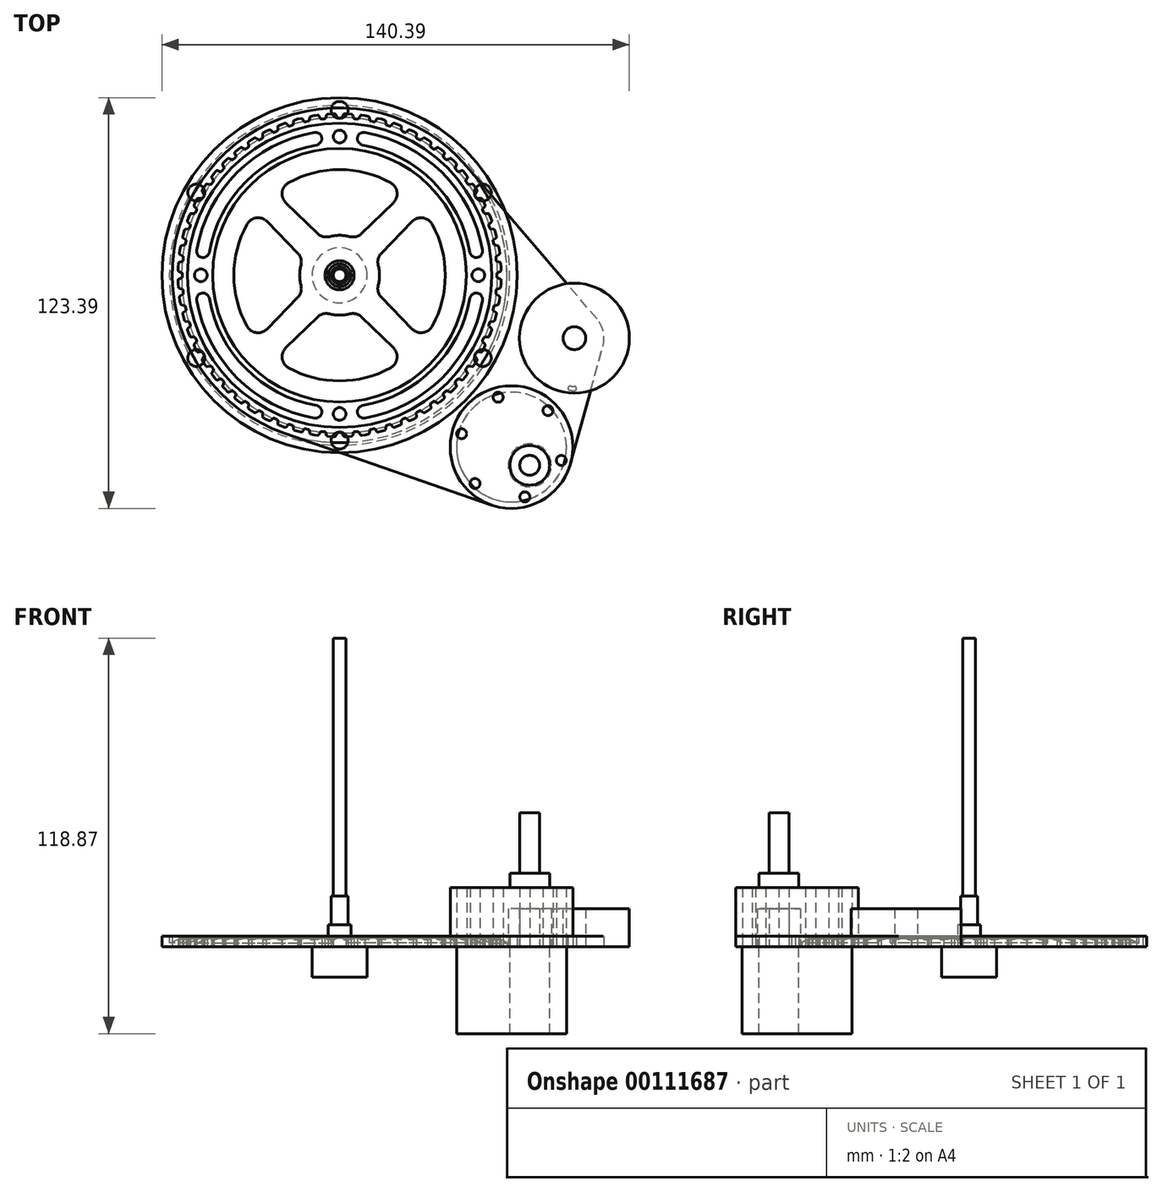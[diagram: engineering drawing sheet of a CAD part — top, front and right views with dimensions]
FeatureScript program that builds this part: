
annotation { "Feature Type Name" : "Feature", "Feature Type Description" : "" }
export const myFeature = defineFeature(function(context is Context, id is Id, definition is map)
    precondition{}
    {
        {
            var Q0;
            Q0=qCreatedBy(makeId("Top.planeOp"),FACE);
            var sketch = newSketch(context, id + "F0", { "sketchPlane" : qUnion([Q0])});
            skCircle(sketch, "E0", {"center": v(0, 0) * mm, "radius": 38.1 * mm});
            skCircle(sketch, "E1.0", {"center": v(0, 0) * mm, "radius": 45.72 * mm});
            skCircle(sketch, "E2", {"center": v(0, 41.68) * mm, "radius": 1.9 * mm});
            skArc(sketch, "E3.1.0", {"start": v(7.57, 42.92) * mm, "mid": v(5.36, 41.38) * mm, "end": v(6.9, 39.17) * mm});
            skLineSegment(sketch, "E3.anchor1", {"start": v(0, 0) * mm, "end": v(0, 41.68) * mm, "construction": true});
            skLineSegment(sketch, "E3.anchor2", {"start": v(0, 0) * mm, "end": v(7.24, 41.05) * mm, "construction": true});
            skArc(sketch, "E4.1.0", {"start": v(39.17, 6.9) * mm, "mid": v(41.38, 5.36) * mm, "end": v(42.92, 7.57) * mm});
            skLineSegment(sketch, "E4.anchor2", {"start": v(0, 0) * mm, "end": v(41.05, 7.24) * mm, "construction": true});
            skArc(sketch, "E5", {"start": v(7.57, 42.92) * mm, "mid": v(30.82, 30.82) * mm, "end": v(42.92, 7.57) * mm});
            skArc(sketch, "E6", {"start": v(6.9, 39.17) * mm, "mid": v(28.12, 28.12) * mm, "end": v(39.17, 6.9) * mm});
            skCircle(sketch, "E7.1.0", {"center": v(-41.68, 0) * mm, "radius": 1.9 * mm});
            skArc(sketch, "E7.1.1", {"start": v(-39.17, 6.9) * mm, "mid": v(-28.12, 28.12) * mm, "end": v(-6.9, 39.17) * mm});
            skArc(sketch, "E7.1.2", {"start": v(-42.92, 7.57) * mm, "mid": v(-30.82, 30.82) * mm, "end": v(-7.57, 42.92) * mm});
            skArc(sketch, "E7.1.3", {"start": v(-42.92, 7.57) * mm, "mid": v(-41.38, 5.36) * mm, "end": v(-39.17, 6.9) * mm});
            skArc(sketch, "E7.1.4", {"start": v(-6.9, 39.17) * mm, "mid": v(-5.36, 41.38) * mm, "end": v(-7.57, 42.92) * mm});
            skCircle(sketch, "E7.2.0", {"center": v(0, -41.68) * mm, "radius": 1.9 * mm});
            skArc(sketch, "E7.2.1", {"start": v(-6.9, -39.17) * mm, "mid": v(-28.12, -28.12) * mm, "end": v(-39.17, -6.9) * mm});
            skArc(sketch, "E7.2.2", {"start": v(-7.57, -42.92) * mm, "mid": v(-30.82, -30.82) * mm, "end": v(-42.92, -7.57) * mm});
            skArc(sketch, "E7.2.3", {"start": v(-7.57, -42.92) * mm, "mid": v(-5.36, -41.38) * mm, "end": v(-6.9, -39.17) * mm});
            skArc(sketch, "E7.2.4", {"start": v(-39.17, -6.9) * mm, "mid": v(-41.38, -5.36) * mm, "end": v(-42.92, -7.57) * mm});
            skCircle(sketch, "E7.3.0", {"center": v(41.68, 0) * mm, "radius": 1.9 * mm});
            skArc(sketch, "E7.3.1", {"start": v(39.17, -6.9) * mm, "mid": v(28.12, -28.12) * mm, "end": v(6.9, -39.17) * mm});
            skArc(sketch, "E7.3.2", {"start": v(42.92, -7.57) * mm, "mid": v(30.82, -30.82) * mm, "end": v(7.57, -42.92) * mm});
            skArc(sketch, "E7.3.3", {"start": v(42.92, -7.57) * mm, "mid": v(41.38, -5.36) * mm, "end": v(39.17, -6.9) * mm});
            skArc(sketch, "E7.3.4", {"start": v(6.9, -39.17) * mm, "mid": v(5.36, -41.38) * mm, "end": v(7.57, -42.92) * mm});
            skCircle(sketch, "E8.0", {"center": v(0, 0) * mm, "radius": 53.34 * mm});
            skCircle(sketch, "E9", {"center": v(0, -49.7) * mm, "radius": 2.54 * mm});
            skCircle(sketch, "E10.1.0", {"center": v(43.04, -24.85) * mm, "radius": 2.54 * mm});
            skCircle(sketch, "E10.2.0", {"center": v(43.04, 24.85) * mm, "radius": 2.54 * mm});
            skCircle(sketch, "E10.3.0", {"center": v(0, 49.7) * mm, "radius": 2.54 * mm});
            skCircle(sketch, "E10.4.0", {"center": v(-43.04, 24.85) * mm, "radius": 2.54 * mm});
            skCircle(sketch, "E10.5.0", {"center": v(-43.04, -24.85) * mm, "radius": 2.54 * mm});
            skCircle(sketch, "E11", {"center": v(0, 0) * mm, "radius": 4.38 * mm});
            skArc(sketch, "E12.0", {"start": v(-11.6, 3.04) * mm, "mid": v(-12, 0) * mm, "end": v(-11.6, -3.04) * mm});
            skArc(sketch, "E13.0", {"start": v(-27.81, 15.31) * mm, "mid": v(-31.75, 0) * mm, "end": v(-27.81, -15.31) * mm});
            skLineSegment(sketch, "E14", {"start": v(-12.56, 6.66) * mm, "end": v(-21.74, 16.13) * mm});
            skLineSegment(sketch, "E15", {"start": v(0, 0) * mm, "end": v(-12, 0) * mm, "construction": true});
            skLineSegment(sketch, "E16.MirrorCS", {"start": v(-12.56, -6.66) * mm, "end": v(-21.74, -16.13) * mm});
            skPoint(sketch, "E17.visualSharp", {"position": v(-25.04, 19.52) * mm});
            skArc(sketch, "E17.filletArc", {"start": v(-21.74, 16.13) * mm, "mid": v(-24.98, 17.25) * mm, "end": v(-27.81, 15.31) * mm});
            skPoint(sketch, "E18.visualSharp", {"position": v(-25.04, -19.52) * mm});
            skArc(sketch, "E18.filletArc", {"start": v(-27.81, -15.31) * mm, "mid": v(-24.98, -17.25) * mm, "end": v(-21.74, -16.13) * mm});
            skPoint(sketch, "E19.visualSharp", {"position": v(-10.92, 4.97) * mm});
            skArc(sketch, "E19.filletArc", {"start": v(-11.6, 3.04) * mm, "mid": v(-11.61, 4.97) * mm, "end": v(-12.56, 6.66) * mm});
            skPoint(sketch, "E20.visualSharp", {"position": v(-10.92, -4.97) * mm});
            skArc(sketch, "E20.filletArc", {"start": v(-12.56, -6.66) * mm, "mid": v(-11.61, -4.97) * mm, "end": v(-11.6, -3.04) * mm});
            skLineSegment(sketch, "E21.1.0", {"start": v(-6.66, -12.56) * mm, "end": v(-16.13, -21.74) * mm});
            skArc(sketch, "E21.1.1", {"start": v(-16.13, -21.74) * mm, "mid": v(-17.25, -24.98) * mm, "end": v(-15.31, -27.81) * mm});
            skArc(sketch, "E21.1.2", {"start": v(-15.31, -27.81) * mm, "mid": v(0, -31.75) * mm, "end": v(15.31, -27.81) * mm});
            skArc(sketch, "E21.1.3", {"start": v(15.31, -27.81) * mm, "mid": v(17.25, -24.98) * mm, "end": v(16.13, -21.74) * mm});
            skLineSegment(sketch, "E21.1.4", {"start": v(6.66, -12.56) * mm, "end": v(16.13, -21.74) * mm});
            skArc(sketch, "E21.1.5", {"start": v(6.66, -12.56) * mm, "mid": v(4.97, -11.61) * mm, "end": v(3.04, -11.6) * mm});
            skArc(sketch, "E21.1.6", {"start": v(-3.04, -11.6) * mm, "mid": v(0, -12) * mm, "end": v(3.04, -11.6) * mm});
            skArc(sketch, "E21.1.7", {"start": v(-3.04, -11.6) * mm, "mid": v(-4.97, -11.61) * mm, "end": v(-6.66, -12.56) * mm});
            skLineSegment(sketch, "E21.2.0", {"start": v(12.56, -6.66) * mm, "end": v(21.74, -16.13) * mm});
            skArc(sketch, "E21.2.1", {"start": v(21.74, -16.13) * mm, "mid": v(24.98, -17.25) * mm, "end": v(27.81, -15.31) * mm});
            skArc(sketch, "E21.2.2", {"start": v(27.81, -15.31) * mm, "mid": v(31.75, 0) * mm, "end": v(27.81, 15.31) * mm});
            skArc(sketch, "E21.2.3", {"start": v(27.81, 15.31) * mm, "mid": v(24.98, 17.25) * mm, "end": v(21.74, 16.13) * mm});
            skLineSegment(sketch, "E21.2.4", {"start": v(12.56, 6.66) * mm, "end": v(21.74, 16.13) * mm});
            skArc(sketch, "E21.2.5", {"start": v(12.56, 6.66) * mm, "mid": v(11.61, 4.97) * mm, "end": v(11.6, 3.04) * mm});
            skArc(sketch, "E21.2.6", {"start": v(11.6, -3.04) * mm, "mid": v(12, 0) * mm, "end": v(11.6, 3.04) * mm});
            skArc(sketch, "E21.2.7", {"start": v(11.6, -3.04) * mm, "mid": v(11.61, -4.97) * mm, "end": v(12.56, -6.66) * mm});
            skLineSegment(sketch, "E21.3.0", {"start": v(6.66, 12.56) * mm, "end": v(16.13, 21.74) * mm});
            skArc(sketch, "E21.3.1", {"start": v(16.13, 21.74) * mm, "mid": v(17.25, 24.98) * mm, "end": v(15.31, 27.81) * mm});
            skArc(sketch, "E21.3.2", {"start": v(15.31, 27.81) * mm, "mid": v(0, 31.75) * mm, "end": v(-15.31, 27.81) * mm});
            skArc(sketch, "E21.3.3", {"start": v(-15.31, 27.81) * mm, "mid": v(-17.25, 24.98) * mm, "end": v(-16.13, 21.74) * mm});
            skLineSegment(sketch, "E21.3.4", {"start": v(-6.66, 12.56) * mm, "end": v(-16.13, 21.74) * mm});
            skArc(sketch, "E21.3.5", {"start": v(-6.66, 12.56) * mm, "mid": v(-4.97, 11.61) * mm, "end": v(-3.04, 11.6) * mm});
            skArc(sketch, "E21.3.6", {"start": v(3.04, 11.6) * mm, "mid": v(0, 12) * mm, "end": v(-3.04, 11.6) * mm});
            skArc(sketch, "E21.3.7", {"start": v(3.04, 11.6) * mm, "mid": v(4.97, 11.61) * mm, "end": v(6.66, 12.56) * mm});
            skSolve(sketch);
        }
        {
            var Q0;
            Q0=makeQuery(id+"F0.imprint","IMPRINT",FACE,{"disambiguationData":[TD([[makeQuery(id+"F0.imprint","IMPRINT",EDGE,{"derivedFrom":sQuery(id+"F0.wireOp",EDGE,"E0")}),-1.0]])]});
            extrude(context, id + "F1", {"entities" : qUnion([Q0]), "depth" : 3.17 * mm});
        }
        {
            var Q0;
            Q0=qCreatedBy(makeId("Top.planeOp"),FACE);
            var sketch = newSketch(context, id + "F2", { "sketchPlane" : qUnion([Q0])});
            skCircle(sketch, "E22", {"center": v(0, 0) * mm, "radius": 1.9 * mm});
            skSolve(sketch);
        }
        {
            var Q0;
            Q0=makeQuery(id+"F2.imprint","IMPRINT",FACE,{"disambiguationData":[TD([[makeQuery(id+"F2.imprint","IMPRINT",EDGE,{"derivedFrom":sQuery(id+"F2.wireOp",EDGE,"E22")}),1.0]])]});
            extrude(context, id + "F3", {"entities" : qUnion([Q0]), "depth" : 76.2 * mm});
        }
        {
            var Q0;
            Q0=makeQuery(id+"F2.imprint","IMPRINT",FACE,{"disambiguationData":[TD([[makeQuery(id+"F2.imprint","IMPRINT",EDGE,{"derivedFrom":sQuery(id+"F2.wireOp",EDGE,"E22")}),1.0]])]});
            extrude(context, id + "F4", {"entities" : qUnion([Q0]), "depth" : 63.5 * mm});
        }
        {
            var Q0;
            Q0=makeQuery(id+"F0.imprint","IMPRINT",FACE,{"disambiguationData":[TD([[makeQuery(id+"F0.imprint","IMPRINT",EDGE,{"derivedFrom":sQuery(id+"F0.wireOp",EDGE,"E0")}),-1.0]])]});
            var Q1;
            Q1=makeQuery(id+"F0.imprint","IMPRINT",FACE,{"disambiguationData":[TD([[makeQuery(id+"F0.imprint","IMPRINT",EDGE,{"derivedFrom":sQuery(id+"F0.wireOp",EDGE,"E7.3.1")}),1.0]])]});
            var Q2;
            Q2=makeQuery(id+"F0.imprint","IMPRINT",FACE,{"disambiguationData":[TD([[makeQuery(id+"F0.imprint","IMPRINT",EDGE,{"derivedFrom":sQuery(id+"F0.wireOp",EDGE,"E7.2.1")}),1.0]])]});
            var Q3;
            Q3=makeQuery(id+"F0.imprint","IMPRINT",FACE,{"disambiguationData":[TD([[makeQuery(id+"F0.imprint","IMPRINT",EDGE,{"derivedFrom":sQuery(id+"F0.wireOp",EDGE,"E3.1.0")}),1.0]])]});
            var Q4;
            Q4=makeQuery(id+"F0.imprint","IMPRINT",FACE,{"disambiguationData":[TD([[makeQuery(id+"F0.imprint","IMPRINT",EDGE,{"derivedFrom":sQuery(id+"F0.wireOp",EDGE,"E7.1.1")}),1.0]])]});
            extrude(context, id + "F5", {"entities" : qUnion([Q0, Q1, Q2, Q3, Q4]), "depth" : 3.17 * mm});
        }
        {
            var Q0;
            Q0=makeQuery(id+"F0.imprint","IMPRINT",FACE,{"disambiguationData":[TD([[makeQuery(id+"F0.imprint","IMPRINT",EDGE,{"derivedFrom":sQuery(id+"F0.wireOp",EDGE,"E1.0")}),-1.0]])]});
            extrude(context, id + "F6", {"entities" : qUnion([Q0]), "depth" : 3.17 * mm});
        }
        {
            var Q0;
            Q0=makeQuery(id+"F0.imprint","IMPRINT",FACE,{"disambiguationData":[TD([[makeQuery(id+"F0.imprint","IMPRINT",EDGE,{"derivedFrom":sQuery(id+"F0.wireOp",EDGE,"E0")}),1.0]])]});
            var Q1;
            Q1=makeQuery(id+"F0.imprint","IMPRINT",FACE,{"disambiguationData":[TD([[makeQuery(id+"F0.imprint","IMPRINT",EDGE,{"derivedFrom":sQuery(id+"F0.wireOp",EDGE,"E0")}),-1.0]])]});
            extrude(context, id + "F7", {"entities" : qUnion([Q0, Q1]), "depth" : 3.17 * mm});
        }
        {
            var Q0;
            Q0=qCreatedBy(makeId("Top.planeOp"),FACE);
            var sketch = newSketch(context, id + "F8", { "sketchPlane" : qUnion([Q0])});
            skCircle(sketch, "E23.0.0", {"center": v(0, 0) * mm, "radius": 45.72 * mm});
            skArc(sketch, "E24.0.0", {"start": v(-42.92, 7.57) * mm, "mid": v(-41.38, 5.36) * mm, "end": v(-39.17, 6.9) * mm});
            skArc(sketch, "E24.0.1", {"start": v(-39.17, 6.9) * mm, "mid": v(-28.12, 28.12) * mm, "end": v(-6.9, 39.17) * mm});
            skArc(sketch, "E24.0.2", {"start": v(-6.9, 39.17) * mm, "mid": v(-5.36, 41.38) * mm, "end": v(-7.57, 42.92) * mm});
            skArc(sketch, "E24.0.3", {"start": v(-7.57, 42.92) * mm, "mid": v(-30.82, 30.82) * mm, "end": v(-42.92, 7.57) * mm});
            skArc(sketch, "E25.0", {"start": v(6.9, 39.17) * mm, "mid": v(28.12, 28.12) * mm, "end": v(39.17, 6.9) * mm});
            skArc(sketch, "E26.0.0", {"start": v(42.92, 7.57) * mm, "mid": v(30.82, 30.82) * mm, "end": v(7.57, 42.92) * mm});
            skArc(sketch, "E26.0.1", {"start": v(7.57, 42.92) * mm, "mid": v(5.36, 41.38) * mm, "end": v(6.9, 39.17) * mm});
            skArc(sketch, "E26.0.3", {"start": v(39.17, 6.9) * mm, "mid": v(41.38, 5.36) * mm, "end": v(42.92, 7.57) * mm});
            skCircle(sketch, "E27.0", {"center": v(0, 41.68) * mm, "radius": 1.9 * mm});
            skCircle(sketch, "E28.0", {"center": v(-41.68, 0) * mm, "radius": 1.9 * mm});
            skArc(sketch, "E29.0.0", {"start": v(-7.57, -42.92) * mm, "mid": v(-5.36, -41.38) * mm, "end": v(-6.9, -39.17) * mm});
            skArc(sketch, "E29.0.1", {"start": v(-6.9, -39.17) * mm, "mid": v(-28.12, -28.12) * mm, "end": v(-39.17, -6.9) * mm});
            skArc(sketch, "E29.0.2", {"start": v(-39.17, -6.9) * mm, "mid": v(-41.38, -5.36) * mm, "end": v(-42.92, -7.57) * mm});
            skArc(sketch, "E29.0.3", {"start": v(-42.92, -7.57) * mm, "mid": v(-30.82, -30.82) * mm, "end": v(-7.57, -42.92) * mm});
            skArc(sketch, "E30.0.0", {"start": v(42.92, -7.57) * mm, "mid": v(41.38, -5.36) * mm, "end": v(39.17, -6.9) * mm});
            skArc(sketch, "E30.0.1", {"start": v(39.17, -6.9) * mm, "mid": v(28.12, -28.12) * mm, "end": v(6.9, -39.17) * mm});
            skArc(sketch, "E30.0.2", {"start": v(6.9, -39.17) * mm, "mid": v(5.36, -41.38) * mm, "end": v(7.57, -42.92) * mm});
            skArc(sketch, "E30.0.3", {"start": v(7.57, -42.92) * mm, "mid": v(30.82, -30.82) * mm, "end": v(42.92, -7.57) * mm});
            skCircle(sketch, "E31.0", {"center": v(41.68, 0) * mm, "radius": 1.9 * mm});
            skCircle(sketch, "E32.0", {"center": v(0, -41.68) * mm, "radius": 1.9 * mm});
            skCircle(sketch, "E33.0", {"center": v(0, 0) * mm, "radius": 38.1 * mm});
            skCircle(sketch, "E34.0", {"center": v(0, 0) * mm, "radius": 49.02 * mm});
            skLineSegment(sketch, "E35", {"start": v(0, 47.24) * mm, "end": v(0.44, 47.24) * mm});
            skLineSegment(sketch, "E36", {"start": v(0.79, 47.46) * mm, "end": v(1.18, 48.3) * mm});
            skLineSegment(sketch, "E37", {"start": v(1.52, 48.51) * mm, "end": v(3.05, 48.51) * mm});
            skLineSegment(sketch, "E38", {"start": v(3.05, 48.51) * mm, "end": v(3.05, 49.53) * mm});
            skLineSegment(sketch, "E39", {"start": v(3.05, 49.53) * mm, "end": v(0, 49.53) * mm});
            skLineSegment(sketch, "E40", {"start": v(0, 49.53) * mm, "end": v(0, 47.24) * mm});
            skPoint(sketch, "E41.visualSharp", {"position": v(0.69, 47.24) * mm});
            skArc(sketch, "E41.filletArc", {"start": v(0.44, 47.24) * mm, "mid": v(0.65, 47.3) * mm, "end": v(0.79, 47.46) * mm});
            skPoint(sketch, "E42.visualSharp", {"position": v(1.28, 48.51) * mm});
            skArc(sketch, "E42.filletArc", {"start": v(1.52, 48.51) * mm, "mid": v(1.32, 48.45) * mm, "end": v(1.18, 48.3) * mm});
            skLineSegment(sketch, "E43.MirrorCS", {"start": v(-3.05, 49.53) * mm, "end": v(0, 49.53) * mm});
            skLineSegment(sketch, "E44.MirrorCS", {"start": v(-3.05, 48.51) * mm, "end": v(-3.05, 49.53) * mm});
            skLineSegment(sketch, "E45.MirrorCS", {"start": v(-1.52, 48.51) * mm, "end": v(-3.05, 48.51) * mm});
            skArc(sketch, "E46.MirrorCS", {"start": v(-1.52, 48.51) * mm, "mid": v(-1.32, 48.45) * mm, "end": v(-1.18, 48.3) * mm});
            skLineSegment(sketch, "E47.MirrorCS", {"start": v(-0.79, 47.46) * mm, "end": v(-1.18, 48.3) * mm});
            skArc(sketch, "E48.MirrorCS", {"start": v(-0.44, 47.24) * mm, "mid": v(-0.65, 47.3) * mm, "end": v(-0.79, 47.46) * mm});
            skLineSegment(sketch, "E49.MirrorCS", {"start": v(0, 47.24) * mm, "end": v(-0.44, 47.24) * mm});
            skLineSegment(sketch, "E50.1.0", {"start": v(-4.94, 46.99) * mm, "end": v(-4.5, 47.03) * mm});
            skArc(sketch, "E50.1.1", {"start": v(-4.5, 47.03) * mm, "mid": v(-4.3, 47.11) * mm, "end": v(-4.18, 47.29) * mm});
            skLineSegment(sketch, "E50.1.2", {"start": v(-4.18, 47.29) * mm, "end": v(-3.88, 48.15) * mm});
            skArc(sketch, "E50.1.3", {"start": v(-3.56, 48.4) * mm, "mid": v(-3.76, 48.33) * mm, "end": v(-3.88, 48.15) * mm});
            skLineSegment(sketch, "E50.1.4", {"start": v(-3.56, 48.4) * mm, "end": v(-2.04, 48.57) * mm});
            skLineSegment(sketch, "E50.1.5", {"start": v(-2.04, 48.57) * mm, "end": v(-2.15, 49.58) * mm});
            skLineSegment(sketch, "E50.1.6", {"start": v(-2.15, 49.58) * mm, "end": v(-5.18, 49.26) * mm});
            skLineSegment(sketch, "E50.1.7", {"start": v(-8.2, 48.94) * mm, "end": v(-5.18, 49.26) * mm});
            skLineSegment(sketch, "E50.1.8", {"start": v(-8.1, 47.93) * mm, "end": v(-8.2, 48.94) * mm});
            skLineSegment(sketch, "E50.1.9", {"start": v(-6.58, 48.09) * mm, "end": v(-8.1, 47.93) * mm});
            skArc(sketch, "E50.1.10", {"start": v(-6.58, 48.09) * mm, "mid": v(-6.37, 48.05) * mm, "end": v(-6.22, 47.9) * mm});
            skLineSegment(sketch, "E50.1.11", {"start": v(-5.75, 47.12) * mm, "end": v(-6.22, 47.9) * mm});
            skArc(sketch, "E50.1.12", {"start": v(-5.38, 46.94) * mm, "mid": v(-5.59, 46.98) * mm, "end": v(-5.75, 47.12) * mm});
            skLineSegment(sketch, "E50.1.13", {"start": v(-4.94, 46.99) * mm, "end": v(-5.38, 46.94) * mm});
            skLineSegment(sketch, "E50.2.0", {"start": v(-9.82, 46.21) * mm, "end": v(-9.39, 46.3) * mm});
            skArc(sketch, "E50.2.1", {"start": v(-9.39, 46.3) * mm, "mid": v(-9.2, 46.4) * mm, "end": v(-9.1, 46.6) * mm});
            skLineSegment(sketch, "E50.2.2", {"start": v(-9.1, 46.6) * mm, "end": v(-8.9, 47.48) * mm});
            skArc(sketch, "E50.2.3", {"start": v(-8.6, 47.77) * mm, "mid": v(-8.79, 47.67) * mm, "end": v(-8.9, 47.48) * mm});
            skLineSegment(sketch, "E50.2.4", {"start": v(-8.6, 47.77) * mm, "end": v(-7.1, 48.09) * mm});
            skLineSegment(sketch, "E50.2.5", {"start": v(-7.1, 48.09) * mm, "end": v(-7.32, 49.08) * mm});
            skLineSegment(sketch, "E50.2.6", {"start": v(-7.32, 49.08) * mm, "end": v(-10.3, 48.45) * mm});
            skLineSegment(sketch, "E50.2.7", {"start": v(-13.28, 47.81) * mm, "end": v(-10.3, 48.45) * mm});
            skLineSegment(sketch, "E50.2.8", {"start": v(-13.07, 46.82) * mm, "end": v(-13.28, 47.81) * mm});
            skLineSegment(sketch, "E50.2.9", {"start": v(-11.57, 47.14) * mm, "end": v(-13.07, 46.82) * mm});
            skArc(sketch, "E50.2.10", {"start": v(-11.57, 47.14) * mm, "mid": v(-11.36, 47.12) * mm, "end": v(-11.2, 47) * mm});
            skLineSegment(sketch, "E50.2.11", {"start": v(-10.64, 46.26) * mm, "end": v(-11.2, 47) * mm});
            skArc(sketch, "E50.2.12", {"start": v(-10.26, 46.12) * mm, "mid": v(-10.47, 46.14) * mm, "end": v(-10.64, 46.26) * mm});
            skLineSegment(sketch, "E50.2.13", {"start": v(-9.82, 46.21) * mm, "end": v(-10.26, 46.12) * mm});
            skLineSegment(sketch, "E50.3.0", {"start": v(-14.6, 44.93) * mm, "end": v(-14.18, 45.07) * mm});
            skArc(sketch, "E50.3.1", {"start": v(-14.18, 45.07) * mm, "mid": v(-14, 45.19) * mm, "end": v(-13.92, 45.38) * mm});
            skLineSegment(sketch, "E50.3.2", {"start": v(-13.92, 45.38) * mm, "end": v(-13.8, 46.3) * mm});
            skArc(sketch, "E50.3.3", {"start": v(-13.55, 46.6) * mm, "mid": v(-13.72, 46.49) * mm, "end": v(-13.8, 46.3) * mm});
            skLineSegment(sketch, "E50.3.4", {"start": v(-13.55, 46.6) * mm, "end": v(-12.1, 47.08) * mm});
            skLineSegment(sketch, "E50.3.5", {"start": v(-12.1, 47.08) * mm, "end": v(-12.4, 48.05) * mm});
            skLineSegment(sketch, "E50.3.6", {"start": v(-12.4, 48.05) * mm, "end": v(-15.3, 47.1) * mm});
            skLineSegment(sketch, "E50.3.7", {"start": v(-18.2, 46.16) * mm, "end": v(-15.3, 47.1) * mm});
            skLineSegment(sketch, "E50.3.8", {"start": v(-17.9, 45.2) * mm, "end": v(-18.2, 46.16) * mm});
            skLineSegment(sketch, "E50.3.9", {"start": v(-16.44, 45.67) * mm, "end": v(-17.9, 45.2) * mm});
            skArc(sketch, "E50.3.10", {"start": v(-16.44, 45.67) * mm, "mid": v(-16.22, 45.68) * mm, "end": v(-16.04, 45.57) * mm});
            skLineSegment(sketch, "E50.3.11", {"start": v(-15.42, 44.9) * mm, "end": v(-16.04, 45.57) * mm});
            skArc(sketch, "E50.3.12", {"start": v(-15.02, 44.8) * mm, "mid": v(-15.23, 44.79) * mm, "end": v(-15.42, 44.9) * mm});
            skLineSegment(sketch, "E50.3.13", {"start": v(-14.6, 44.93) * mm, "end": v(-15.02, 44.8) * mm});
            skLineSegment(sketch, "E50.4.0", {"start": v(-19.22, 43.16) * mm, "end": v(-18.81, 43.34) * mm});
            skArc(sketch, "E50.4.1", {"start": v(-18.81, 43.34) * mm, "mid": v(-18.65, 43.48) * mm, "end": v(-18.59, 43.68) * mm});
            skLineSegment(sketch, "E50.4.2", {"start": v(-18.59, 43.68) * mm, "end": v(-18.57, 44.6) * mm});
            skArc(sketch, "E50.4.3", {"start": v(-18.34, 44.94) * mm, "mid": v(-18.5, 44.8) * mm, "end": v(-18.57, 44.6) * mm});
            skLineSegment(sketch, "E50.4.4", {"start": v(-18.34, 44.94) * mm, "end": v(-16.95, 45.56) * mm});
            skLineSegment(sketch, "E50.4.5", {"start": v(-16.95, 45.56) * mm, "end": v(-17.36, 46.49) * mm});
            skLineSegment(sketch, "E50.4.6", {"start": v(-17.36, 46.49) * mm, "end": v(-20.15, 45.25) * mm});
            skLineSegment(sketch, "E50.4.7", {"start": v(-22.93, 44) * mm, "end": v(-20.15, 45.25) * mm});
            skLineSegment(sketch, "E50.4.8", {"start": v(-22.52, 43.08) * mm, "end": v(-22.93, 44) * mm});
            skLineSegment(sketch, "E50.4.9", {"start": v(-21.12, 43.7) * mm, "end": v(-22.52, 43.08) * mm});
            skArc(sketch, "E50.4.10", {"start": v(-21.12, 43.7) * mm, "mid": v(-20.91, 43.73) * mm, "end": v(-20.72, 43.64) * mm});
            skLineSegment(sketch, "E50.4.11", {"start": v(-20.03, 43.04) * mm, "end": v(-20.72, 43.64) * mm});
            skArc(sketch, "E50.4.12", {"start": v(-19.62, 42.98) * mm, "mid": v(-19.83, 42.95) * mm, "end": v(-20.03, 43.04) * mm});
            skLineSegment(sketch, "E50.4.13", {"start": v(-19.22, 43.16) * mm, "end": v(-19.62, 42.98) * mm});
            skLineSegment(sketch, "E50.5.0", {"start": v(-23.62, 40.91) * mm, "end": v(-23.24, 41.14) * mm});
            skArc(sketch, "E50.5.1", {"start": v(-23.24, 41.14) * mm, "mid": v(-23.1, 41.3) * mm, "end": v(-23.05, 41.5) * mm});
            skLineSegment(sketch, "E50.5.2", {"start": v(-23.05, 41.5) * mm, "end": v(-23.13, 42.41) * mm});
            skArc(sketch, "E50.5.3", {"start": v(-22.94, 42.77) * mm, "mid": v(-23.09, 42.62) * mm, "end": v(-23.13, 42.41) * mm});
            skLineSegment(sketch, "E50.5.4", {"start": v(-22.94, 42.77) * mm, "end": v(-21.62, 43.54) * mm});
            skLineSegment(sketch, "E50.5.5", {"start": v(-21.62, 43.54) * mm, "end": v(-22.13, 44.42) * mm});
            skLineSegment(sketch, "E50.5.6", {"start": v(-22.13, 44.42) * mm, "end": v(-24.77, 42.9) * mm});
            skLineSegment(sketch, "E50.5.7", {"start": v(-27.4, 41.37) * mm, "end": v(-24.77, 42.9) * mm});
            skLineSegment(sketch, "E50.5.8", {"start": v(-26.9, 40.5) * mm, "end": v(-27.4, 41.37) * mm});
            skLineSegment(sketch, "E50.5.9", {"start": v(-25.57, 41.25) * mm, "end": v(-26.9, 40.5) * mm});
            skArc(sketch, "E50.5.10", {"start": v(-25.57, 41.25) * mm, "mid": v(-25.37, 41.3) * mm, "end": v(-25.16, 41.24) * mm});
            skLineSegment(sketch, "E50.5.11", {"start": v(-24.41, 40.71) * mm, "end": v(-25.16, 41.24) * mm});
            skArc(sketch, "E50.5.12", {"start": v(-24, 40.7) * mm, "mid": v(-24.21, 40.64) * mm, "end": v(-24.41, 40.71) * mm});
            skLineSegment(sketch, "E50.5.13", {"start": v(-23.62, 40.91) * mm, "end": v(-24, 40.7) * mm});
            skLineSegment(sketch, "E50.6.0", {"start": v(-27.77, 38.22) * mm, "end": v(-27.41, 38.48) * mm});
            skArc(sketch, "E50.6.1", {"start": v(-27.41, 38.48) * mm, "mid": v(-27.28, 38.65) * mm, "end": v(-27.26, 38.86) * mm});
            skLineSegment(sketch, "E50.6.2", {"start": v(-27.26, 38.86) * mm, "end": v(-27.44, 39.76) * mm});
            skArc(sketch, "E50.6.3", {"start": v(-27.29, 40.14) * mm, "mid": v(-27.42, 39.97) * mm, "end": v(-27.44, 39.76) * mm});
            skLineSegment(sketch, "E50.6.4", {"start": v(-27.29, 40.14) * mm, "end": v(-26.05, 41.04) * mm});
            skLineSegment(sketch, "E50.6.5", {"start": v(-26.05, 41.04) * mm, "end": v(-26.65, 41.86) * mm});
            skLineSegment(sketch, "E50.6.6", {"start": v(-26.65, 41.86) * mm, "end": v(-29.11, 40.07) * mm});
            skLineSegment(sketch, "E50.6.7", {"start": v(-31.58, 38.28) * mm, "end": v(-29.11, 40.07) * mm});
            skLineSegment(sketch, "E50.6.8", {"start": v(-30.98, 37.46) * mm, "end": v(-31.58, 38.28) * mm});
            skLineSegment(sketch, "E50.6.9", {"start": v(-29.75, 38.35) * mm, "end": v(-30.98, 37.46) * mm});
            skArc(sketch, "E50.6.10", {"start": v(-29.75, 38.35) * mm, "mid": v(-29.55, 38.43) * mm, "end": v(-29.34, 38.38) * mm});
            skLineSegment(sketch, "E50.6.11", {"start": v(-28.54, 37.94) * mm, "end": v(-29.34, 38.38) * mm});
            skArc(sketch, "E50.6.12", {"start": v(-28.13, 37.96) * mm, "mid": v(-28.33, 37.89) * mm, "end": v(-28.54, 37.94) * mm});
            skLineSegment(sketch, "E50.6.13", {"start": v(-27.77, 38.22) * mm, "end": v(-28.13, 37.96) * mm});
            skLineSegment(sketch, "E50.7.0", {"start": v(-31.61, 35.1) * mm, "end": v(-31.28, 35.4) * mm});
            skArc(sketch, "E50.7.1", {"start": v(-31.28, 35.4) * mm, "mid": v(-31.17, 35.59) * mm, "end": v(-31.17, 35.8) * mm});
            skLineSegment(sketch, "E50.7.2", {"start": v(-31.17, 35.8) * mm, "end": v(-31.44, 36.68) * mm});
            skArc(sketch, "E50.7.3", {"start": v(-31.33, 37.07) * mm, "mid": v(-31.44, 36.89) * mm, "end": v(-31.44, 36.68) * mm});
            skLineSegment(sketch, "E50.7.4", {"start": v(-31.33, 37.07) * mm, "end": v(-30.2, 38.1) * mm});
            skLineSegment(sketch, "E50.7.5", {"start": v(-30.2, 38.1) * mm, "end": v(-30.88, 38.85) * mm});
            skLineSegment(sketch, "E50.7.6", {"start": v(-30.88, 38.85) * mm, "end": v(-33.14, 36.8) * mm});
            skLineSegment(sketch, "E50.7.7", {"start": v(-35.4, 34.77) * mm, "end": v(-33.14, 36.8) * mm});
            skLineSegment(sketch, "E50.7.8", {"start": v(-34.73, 34.01) * mm, "end": v(-35.4, 34.77) * mm});
            skLineSegment(sketch, "E50.7.9", {"start": v(-33.6, 35.04) * mm, "end": v(-34.73, 34.01) * mm});
            skArc(sketch, "E50.7.10", {"start": v(-33.6, 35.04) * mm, "mid": v(-33.4, 35.13) * mm, "end": v(-33.19, 35.1) * mm});
            skLineSegment(sketch, "E50.7.11", {"start": v(-32.35, 34.75) * mm, "end": v(-33.19, 35.1) * mm});
            skArc(sketch, "E50.7.12", {"start": v(-31.94, 34.81) * mm, "mid": v(-32.13, 34.72) * mm, "end": v(-32.35, 34.75) * mm});
            skLineSegment(sketch, "E50.7.13", {"start": v(-31.61, 35.1) * mm, "end": v(-31.94, 34.81) * mm});
            skLineSegment(sketch, "E50.8.0", {"start": v(-35.1, 31.61) * mm, "end": v(-34.81, 31.94) * mm});
            skArc(sketch, "E50.8.1", {"start": v(-34.81, 31.94) * mm, "mid": v(-34.72, 32.13) * mm, "end": v(-34.75, 32.35) * mm});
            skLineSegment(sketch, "E50.8.2", {"start": v(-34.75, 32.35) * mm, "end": v(-35.1, 33.19) * mm});
            skArc(sketch, "E50.8.3", {"start": v(-35.04, 33.6) * mm, "mid": v(-35.13, 33.4) * mm, "end": v(-35.1, 33.19) * mm});
            skLineSegment(sketch, "E50.8.4", {"start": v(-35.04, 33.6) * mm, "end": v(-34.01, 34.73) * mm});
            skLineSegment(sketch, "E50.8.5", {"start": v(-34.01, 34.73) * mm, "end": v(-34.77, 35.4) * mm});
            skLineSegment(sketch, "E50.8.6", {"start": v(-34.77, 35.4) * mm, "end": v(-36.8, 33.14) * mm});
            skLineSegment(sketch, "E50.8.7", {"start": v(-38.85, 30.88) * mm, "end": v(-36.8, 33.14) * mm});
            skLineSegment(sketch, "E50.8.8", {"start": v(-38.1, 30.2) * mm, "end": v(-38.85, 30.88) * mm});
            skLineSegment(sketch, "E50.8.9", {"start": v(-37.07, 31.33) * mm, "end": v(-38.1, 30.2) * mm});
            skArc(sketch, "E50.8.10", {"start": v(-37.07, 31.33) * mm, "mid": v(-36.89, 31.44) * mm, "end": v(-36.68, 31.44) * mm});
            skLineSegment(sketch, "E50.8.11", {"start": v(-35.8, 31.17) * mm, "end": v(-36.68, 31.44) * mm});
            skArc(sketch, "E50.8.12", {"start": v(-35.4, 31.28) * mm, "mid": v(-35.59, 31.17) * mm, "end": v(-35.8, 31.17) * mm});
            skLineSegment(sketch, "E50.8.13", {"start": v(-35.1, 31.61) * mm, "end": v(-35.4, 31.28) * mm});
            skLineSegment(sketch, "E50.9.0", {"start": v(-38.22, 27.77) * mm, "end": v(-37.96, 28.13) * mm});
            skArc(sketch, "E50.9.1", {"start": v(-37.96, 28.13) * mm, "mid": v(-37.89, 28.33) * mm, "end": v(-37.94, 28.54) * mm});
            skLineSegment(sketch, "E50.9.2", {"start": v(-37.94, 28.54) * mm, "end": v(-38.38, 29.34) * mm});
            skArc(sketch, "E50.9.3", {"start": v(-38.35, 29.75) * mm, "mid": v(-38.43, 29.55) * mm, "end": v(-38.38, 29.34) * mm});
            skLineSegment(sketch, "E50.9.4", {"start": v(-38.35, 29.75) * mm, "end": v(-37.46, 30.98) * mm});
            skLineSegment(sketch, "E50.9.5", {"start": v(-37.46, 30.98) * mm, "end": v(-38.28, 31.58) * mm});
            skLineSegment(sketch, "E50.9.6", {"start": v(-38.28, 31.58) * mm, "end": v(-40.07, 29.11) * mm});
            skLineSegment(sketch, "E50.9.7", {"start": v(-41.86, 26.65) * mm, "end": v(-40.07, 29.11) * mm});
            skLineSegment(sketch, "E50.9.8", {"start": v(-41.04, 26.05) * mm, "end": v(-41.86, 26.65) * mm});
            skLineSegment(sketch, "E50.9.9", {"start": v(-40.14, 27.29) * mm, "end": v(-41.04, 26.05) * mm});
            skArc(sketch, "E50.9.10", {"start": v(-40.14, 27.29) * mm, "mid": v(-39.97, 27.42) * mm, "end": v(-39.76, 27.44) * mm});
            skLineSegment(sketch, "E50.9.11", {"start": v(-38.86, 27.26) * mm, "end": v(-39.76, 27.44) * mm});
            skArc(sketch, "E50.9.12", {"start": v(-38.48, 27.41) * mm, "mid": v(-38.65, 27.28) * mm, "end": v(-38.86, 27.26) * mm});
            skLineSegment(sketch, "E50.9.13", {"start": v(-38.22, 27.77) * mm, "end": v(-38.48, 27.41) * mm});
            skLineSegment(sketch, "E50.10.0", {"start": v(-40.91, 23.62) * mm, "end": v(-40.7, 24) * mm});
            skArc(sketch, "E50.10.1", {"start": v(-40.7, 24) * mm, "mid": v(-40.64, 24.21) * mm, "end": v(-40.71, 24.41) * mm});
            skLineSegment(sketch, "E50.10.2", {"start": v(-40.71, 24.41) * mm, "end": v(-41.24, 25.16) * mm});
            skArc(sketch, "E50.10.3", {"start": v(-41.25, 25.57) * mm, "mid": v(-41.3, 25.37) * mm, "end": v(-41.24, 25.16) * mm});
            skLineSegment(sketch, "E50.10.4", {"start": v(-41.25, 25.57) * mm, "end": v(-40.5, 26.9) * mm});
            skLineSegment(sketch, "E50.10.5", {"start": v(-40.5, 26.9) * mm, "end": v(-41.37, 27.4) * mm});
            skLineSegment(sketch, "E50.10.6", {"start": v(-41.37, 27.4) * mm, "end": v(-42.9, 24.77) * mm});
            skLineSegment(sketch, "E50.10.7", {"start": v(-44.42, 22.13) * mm, "end": v(-42.9, 24.77) * mm});
            skLineSegment(sketch, "E50.10.8", {"start": v(-43.54, 21.62) * mm, "end": v(-44.42, 22.13) * mm});
            skLineSegment(sketch, "E50.10.9", {"start": v(-42.77, 22.94) * mm, "end": v(-43.54, 21.62) * mm});
            skArc(sketch, "E50.10.10", {"start": v(-42.77, 22.94) * mm, "mid": v(-42.62, 23.09) * mm, "end": v(-42.41, 23.13) * mm});
            skLineSegment(sketch, "E50.10.11", {"start": v(-41.5, 23.05) * mm, "end": v(-42.41, 23.13) * mm});
            skArc(sketch, "E50.10.12", {"start": v(-41.14, 23.24) * mm, "mid": v(-41.3, 23.1) * mm, "end": v(-41.5, 23.05) * mm});
            skLineSegment(sketch, "E50.10.13", {"start": v(-40.91, 23.62) * mm, "end": v(-41.14, 23.24) * mm});
            skLineSegment(sketch, "E50.11.0", {"start": v(-43.16, 19.22) * mm, "end": v(-42.98, 19.62) * mm});
            skArc(sketch, "E50.11.1", {"start": v(-42.98, 19.62) * mm, "mid": v(-42.95, 19.83) * mm, "end": v(-43.04, 20.03) * mm});
            skLineSegment(sketch, "E50.11.2", {"start": v(-43.04, 20.03) * mm, "end": v(-43.64, 20.72) * mm});
            skArc(sketch, "E50.11.3", {"start": v(-43.7, 21.12) * mm, "mid": v(-43.73, 20.91) * mm, "end": v(-43.64, 20.72) * mm});
            skLineSegment(sketch, "E50.11.4", {"start": v(-43.7, 21.12) * mm, "end": v(-43.08, 22.52) * mm});
            skLineSegment(sketch, "E50.11.5", {"start": v(-43.08, 22.52) * mm, "end": v(-44, 22.93) * mm});
            skLineSegment(sketch, "E50.11.6", {"start": v(-44, 22.93) * mm, "end": v(-45.25, 20.15) * mm});
            skLineSegment(sketch, "E50.11.7", {"start": v(-46.49, 17.36) * mm, "end": v(-45.25, 20.15) * mm});
            skLineSegment(sketch, "E50.11.8", {"start": v(-45.56, 16.95) * mm, "end": v(-46.49, 17.36) * mm});
            skLineSegment(sketch, "E50.11.9", {"start": v(-44.94, 18.34) * mm, "end": v(-45.56, 16.95) * mm});
            skArc(sketch, "E50.11.10", {"start": v(-44.94, 18.34) * mm, "mid": v(-44.8, 18.5) * mm, "end": v(-44.6, 18.57) * mm});
            skLineSegment(sketch, "E50.11.11", {"start": v(-43.68, 18.59) * mm, "end": v(-44.6, 18.57) * mm});
            skArc(sketch, "E50.11.12", {"start": v(-43.34, 18.81) * mm, "mid": v(-43.48, 18.65) * mm, "end": v(-43.68, 18.59) * mm});
            skLineSegment(sketch, "E50.11.13", {"start": v(-43.16, 19.22) * mm, "end": v(-43.34, 18.81) * mm});
            skLineSegment(sketch, "E50.12.0", {"start": v(-44.93, 14.6) * mm, "end": v(-44.8, 15.02) * mm});
            skArc(sketch, "E50.12.1", {"start": v(-44.8, 15.02) * mm, "mid": v(-44.79, 15.23) * mm, "end": v(-44.9, 15.42) * mm});
            skLineSegment(sketch, "E50.12.2", {"start": v(-44.9, 15.42) * mm, "end": v(-45.57, 16.04) * mm});
            skArc(sketch, "E50.12.3", {"start": v(-45.67, 16.44) * mm, "mid": v(-45.68, 16.22) * mm, "end": v(-45.57, 16.04) * mm});
            skLineSegment(sketch, "E50.12.4", {"start": v(-45.67, 16.44) * mm, "end": v(-45.2, 17.9) * mm});
            skLineSegment(sketch, "E50.12.5", {"start": v(-45.2, 17.9) * mm, "end": v(-46.16, 18.2) * mm});
            skLineSegment(sketch, "E50.12.6", {"start": v(-46.16, 18.2) * mm, "end": v(-47.1, 15.3) * mm});
            skLineSegment(sketch, "E50.12.7", {"start": v(-48.05, 12.4) * mm, "end": v(-47.1, 15.3) * mm});
            skLineSegment(sketch, "E50.12.8", {"start": v(-47.08, 12.1) * mm, "end": v(-48.05, 12.4) * mm});
            skLineSegment(sketch, "E50.12.9", {"start": v(-46.6, 13.55) * mm, "end": v(-47.08, 12.1) * mm});
            skArc(sketch, "E50.12.10", {"start": v(-46.6, 13.55) * mm, "mid": v(-46.49, 13.72) * mm, "end": v(-46.3, 13.8) * mm});
            skLineSegment(sketch, "E50.12.11", {"start": v(-45.38, 13.92) * mm, "end": v(-46.3, 13.8) * mm});
            skArc(sketch, "E50.12.12", {"start": v(-45.07, 14.18) * mm, "mid": v(-45.19, 14) * mm, "end": v(-45.38, 13.92) * mm});
            skLineSegment(sketch, "E50.12.13", {"start": v(-44.93, 14.6) * mm, "end": v(-45.07, 14.18) * mm});
            skLineSegment(sketch, "E50.13.0", {"start": v(-46.21, 9.82) * mm, "end": v(-46.12, 10.26) * mm});
            skArc(sketch, "E50.13.1", {"start": v(-46.12, 10.26) * mm, "mid": v(-46.14, 10.47) * mm, "end": v(-46.26, 10.64) * mm});
            skLineSegment(sketch, "E50.13.2", {"start": v(-46.26, 10.64) * mm, "end": v(-47, 11.2) * mm});
            skArc(sketch, "E50.13.3", {"start": v(-47.14, 11.57) * mm, "mid": v(-47.12, 11.36) * mm, "end": v(-47, 11.2) * mm});
            skLineSegment(sketch, "E50.13.4", {"start": v(-47.14, 11.57) * mm, "end": v(-46.82, 13.07) * mm});
            skLineSegment(sketch, "E50.13.5", {"start": v(-46.82, 13.07) * mm, "end": v(-47.81, 13.28) * mm});
            skLineSegment(sketch, "E50.13.6", {"start": v(-47.81, 13.28) * mm, "end": v(-48.45, 10.3) * mm});
            skLineSegment(sketch, "E50.13.7", {"start": v(-49.08, 7.32) * mm, "end": v(-48.45, 10.3) * mm});
            skLineSegment(sketch, "E50.13.8", {"start": v(-48.09, 7.1) * mm, "end": v(-49.08, 7.32) * mm});
            skLineSegment(sketch, "E50.13.9", {"start": v(-47.77, 8.6) * mm, "end": v(-48.09, 7.1) * mm});
            skArc(sketch, "E50.13.10", {"start": v(-47.77, 8.6) * mm, "mid": v(-47.67, 8.79) * mm, "end": v(-47.48, 8.9) * mm});
            skLineSegment(sketch, "E50.13.11", {"start": v(-46.6, 9.1) * mm, "end": v(-47.48, 8.9) * mm});
            skArc(sketch, "E50.13.12", {"start": v(-46.3, 9.39) * mm, "mid": v(-46.4, 9.2) * mm, "end": v(-46.6, 9.1) * mm});
            skLineSegment(sketch, "E50.13.13", {"start": v(-46.21, 9.82) * mm, "end": v(-46.3, 9.39) * mm});
            skLineSegment(sketch, "E50.14.0", {"start": v(-46.99, 4.94) * mm, "end": v(-46.94, 5.38) * mm});
            skArc(sketch, "E50.14.1", {"start": v(-46.94, 5.38) * mm, "mid": v(-46.98, 5.59) * mm, "end": v(-47.12, 5.75) * mm});
            skLineSegment(sketch, "E50.14.2", {"start": v(-47.12, 5.75) * mm, "end": v(-47.9, 6.22) * mm});
            skArc(sketch, "E50.14.3", {"start": v(-48.09, 6.58) * mm, "mid": v(-48.05, 6.37) * mm, "end": v(-47.9, 6.22) * mm});
            skLineSegment(sketch, "E50.14.4", {"start": v(-48.09, 6.58) * mm, "end": v(-47.93, 8.1) * mm});
            skLineSegment(sketch, "E50.14.5", {"start": v(-47.93, 8.1) * mm, "end": v(-48.94, 8.2) * mm});
            skLineSegment(sketch, "E50.14.6", {"start": v(-48.94, 8.2) * mm, "end": v(-49.26, 5.18) * mm});
            skLineSegment(sketch, "E50.14.7", {"start": v(-49.58, 2.15) * mm, "end": v(-49.26, 5.18) * mm});
            skLineSegment(sketch, "E50.14.8", {"start": v(-48.57, 2.04) * mm, "end": v(-49.58, 2.15) * mm});
            skLineSegment(sketch, "E50.14.9", {"start": v(-48.4, 3.56) * mm, "end": v(-48.57, 2.04) * mm});
            skArc(sketch, "E50.14.10", {"start": v(-48.4, 3.56) * mm, "mid": v(-48.33, 3.76) * mm, "end": v(-48.15, 3.88) * mm});
            skLineSegment(sketch, "E50.14.11", {"start": v(-47.29, 4.18) * mm, "end": v(-48.15, 3.88) * mm});
            skArc(sketch, "E50.14.12", {"start": v(-47.03, 4.5) * mm, "mid": v(-47.11, 4.3) * mm, "end": v(-47.29, 4.18) * mm});
            skLineSegment(sketch, "E50.14.13", {"start": v(-46.99, 4.94) * mm, "end": v(-47.03, 4.5) * mm});
            skLineSegment(sketch, "E50.15.0", {"start": v(-47.24, 0) * mm, "end": v(-47.24, 0.44) * mm});
            skArc(sketch, "E50.15.1", {"start": v(-47.24, 0.44) * mm, "mid": v(-47.3, 0.65) * mm, "end": v(-47.46, 0.79) * mm});
            skLineSegment(sketch, "E50.15.2", {"start": v(-47.46, 0.79) * mm, "end": v(-48.3, 1.18) * mm});
            skArc(sketch, "E50.15.3", {"start": v(-48.51, 1.52) * mm, "mid": v(-48.45, 1.32) * mm, "end": v(-48.3, 1.18) * mm});
            skLineSegment(sketch, "E50.15.4", {"start": v(-48.51, 1.52) * mm, "end": v(-48.51, 3.05) * mm});
            skLineSegment(sketch, "E50.15.5", {"start": v(-48.51, 3.05) * mm, "end": v(-49.53, 3.05) * mm});
            skLineSegment(sketch, "E50.15.6", {"start": v(-49.53, 3.05) * mm, "end": v(-49.53, 0) * mm});
            skLineSegment(sketch, "E50.15.7", {"start": v(-49.53, -3.05) * mm, "end": v(-49.53, 0) * mm});
            skLineSegment(sketch, "E50.15.8", {"start": v(-48.51, -3.05) * mm, "end": v(-49.53, -3.05) * mm});
            skLineSegment(sketch, "E50.15.9", {"start": v(-48.51, -1.52) * mm, "end": v(-48.51, -3.05) * mm});
            skArc(sketch, "E50.15.10", {"start": v(-48.51, -1.52) * mm, "mid": v(-48.45, -1.32) * mm, "end": v(-48.3, -1.18) * mm});
            skLineSegment(sketch, "E50.15.11", {"start": v(-47.46, -0.79) * mm, "end": v(-48.3, -1.18) * mm});
            skArc(sketch, "E50.15.12", {"start": v(-47.24, -0.44) * mm, "mid": v(-47.3, -0.65) * mm, "end": v(-47.46, -0.79) * mm});
            skLineSegment(sketch, "E50.15.13", {"start": v(-47.24, 0) * mm, "end": v(-47.24, -0.44) * mm});
            skLineSegment(sketch, "E50.16.0", {"start": v(-46.99, -4.94) * mm, "end": v(-47.03, -4.5) * mm});
            skArc(sketch, "E50.16.1", {"start": v(-47.03, -4.5) * mm, "mid": v(-47.11, -4.3) * mm, "end": v(-47.29, -4.18) * mm});
            skLineSegment(sketch, "E50.16.2", {"start": v(-47.29, -4.18) * mm, "end": v(-48.15, -3.88) * mm});
            skArc(sketch, "E50.16.3", {"start": v(-48.4, -3.56) * mm, "mid": v(-48.33, -3.76) * mm, "end": v(-48.15, -3.88) * mm});
            skLineSegment(sketch, "E50.16.4", {"start": v(-48.4, -3.56) * mm, "end": v(-48.57, -2.04) * mm});
            skLineSegment(sketch, "E50.16.5", {"start": v(-48.57, -2.04) * mm, "end": v(-49.58, -2.15) * mm});
            skLineSegment(sketch, "E50.16.6", {"start": v(-49.58, -2.15) * mm, "end": v(-49.26, -5.18) * mm});
            skLineSegment(sketch, "E50.16.7", {"start": v(-48.94, -8.2) * mm, "end": v(-49.26, -5.18) * mm});
            skLineSegment(sketch, "E50.16.8", {"start": v(-47.93, -8.1) * mm, "end": v(-48.94, -8.2) * mm});
            skLineSegment(sketch, "E50.16.9", {"start": v(-48.09, -6.58) * mm, "end": v(-47.93, -8.1) * mm});
            skArc(sketch, "E50.16.10", {"start": v(-48.09, -6.58) * mm, "mid": v(-48.05, -6.37) * mm, "end": v(-47.9, -6.22) * mm});
            skLineSegment(sketch, "E50.16.11", {"start": v(-47.12, -5.75) * mm, "end": v(-47.9, -6.22) * mm});
            skArc(sketch, "E50.16.12", {"start": v(-46.94, -5.38) * mm, "mid": v(-46.98, -5.59) * mm, "end": v(-47.12, -5.75) * mm});
            skLineSegment(sketch, "E50.16.13", {"start": v(-46.99, -4.94) * mm, "end": v(-46.94, -5.38) * mm});
            skLineSegment(sketch, "E50.17.0", {"start": v(-46.21, -9.82) * mm, "end": v(-46.3, -9.39) * mm});
            skArc(sketch, "E50.17.1", {"start": v(-46.3, -9.39) * mm, "mid": v(-46.4, -9.2) * mm, "end": v(-46.6, -9.1) * mm});
            skLineSegment(sketch, "E50.17.2", {"start": v(-46.6, -9.1) * mm, "end": v(-47.48, -8.9) * mm});
            skArc(sketch, "E50.17.3", {"start": v(-47.77, -8.6) * mm, "mid": v(-47.67, -8.79) * mm, "end": v(-47.48, -8.9) * mm});
            skLineSegment(sketch, "E50.17.4", {"start": v(-47.77, -8.6) * mm, "end": v(-48.09, -7.1) * mm});
            skLineSegment(sketch, "E50.17.5", {"start": v(-48.09, -7.1) * mm, "end": v(-49.08, -7.32) * mm});
            skLineSegment(sketch, "E50.17.6", {"start": v(-49.08, -7.32) * mm, "end": v(-48.45, -10.3) * mm});
            skLineSegment(sketch, "E50.17.7", {"start": v(-47.81, -13.28) * mm, "end": v(-48.45, -10.3) * mm});
            skLineSegment(sketch, "E50.17.8", {"start": v(-46.82, -13.07) * mm, "end": v(-47.81, -13.28) * mm});
            skLineSegment(sketch, "E50.17.9", {"start": v(-47.14, -11.57) * mm, "end": v(-46.82, -13.07) * mm});
            skArc(sketch, "E50.17.10", {"start": v(-47.14, -11.57) * mm, "mid": v(-47.12, -11.36) * mm, "end": v(-47, -11.2) * mm});
            skLineSegment(sketch, "E50.17.11", {"start": v(-46.26, -10.64) * mm, "end": v(-47, -11.2) * mm});
            skArc(sketch, "E50.17.12", {"start": v(-46.12, -10.26) * mm, "mid": v(-46.14, -10.47) * mm, "end": v(-46.26, -10.64) * mm});
            skLineSegment(sketch, "E50.17.13", {"start": v(-46.21, -9.82) * mm, "end": v(-46.12, -10.26) * mm});
            skLineSegment(sketch, "E50.18.0", {"start": v(-44.93, -14.6) * mm, "end": v(-45.07, -14.18) * mm});
            skArc(sketch, "E50.18.1", {"start": v(-45.07, -14.18) * mm, "mid": v(-45.19, -14) * mm, "end": v(-45.38, -13.92) * mm});
            skLineSegment(sketch, "E50.18.2", {"start": v(-45.38, -13.92) * mm, "end": v(-46.3, -13.8) * mm});
            skArc(sketch, "E50.18.3", {"start": v(-46.6, -13.55) * mm, "mid": v(-46.49, -13.72) * mm, "end": v(-46.3, -13.8) * mm});
            skLineSegment(sketch, "E50.18.4", {"start": v(-46.6, -13.55) * mm, "end": v(-47.08, -12.1) * mm});
            skLineSegment(sketch, "E50.18.5", {"start": v(-47.08, -12.1) * mm, "end": v(-48.05, -12.4) * mm});
            skLineSegment(sketch, "E50.18.6", {"start": v(-48.05, -12.4) * mm, "end": v(-47.1, -15.3) * mm});
            skLineSegment(sketch, "E50.18.7", {"start": v(-46.16, -18.2) * mm, "end": v(-47.1, -15.3) * mm});
            skLineSegment(sketch, "E50.18.8", {"start": v(-45.2, -17.9) * mm, "end": v(-46.16, -18.2) * mm});
            skLineSegment(sketch, "E50.18.9", {"start": v(-45.67, -16.44) * mm, "end": v(-45.2, -17.9) * mm});
            skArc(sketch, "E50.18.10", {"start": v(-45.67, -16.44) * mm, "mid": v(-45.68, -16.22) * mm, "end": v(-45.57, -16.04) * mm});
            skLineSegment(sketch, "E50.18.11", {"start": v(-44.9, -15.42) * mm, "end": v(-45.57, -16.04) * mm});
            skArc(sketch, "E50.18.12", {"start": v(-44.8, -15.02) * mm, "mid": v(-44.79, -15.23) * mm, "end": v(-44.9, -15.42) * mm});
            skLineSegment(sketch, "E50.18.13", {"start": v(-44.93, -14.6) * mm, "end": v(-44.8, -15.02) * mm});
            skLineSegment(sketch, "E50.19.0", {"start": v(-43.16, -19.22) * mm, "end": v(-43.34, -18.81) * mm});
            skArc(sketch, "E50.19.1", {"start": v(-43.34, -18.81) * mm, "mid": v(-43.48, -18.65) * mm, "end": v(-43.68, -18.59) * mm});
            skLineSegment(sketch, "E50.19.2", {"start": v(-43.68, -18.59) * mm, "end": v(-44.6, -18.57) * mm});
            skArc(sketch, "E50.19.3", {"start": v(-44.94, -18.34) * mm, "mid": v(-44.8, -18.5) * mm, "end": v(-44.6, -18.57) * mm});
            skLineSegment(sketch, "E50.19.4", {"start": v(-44.94, -18.34) * mm, "end": v(-45.56, -16.95) * mm});
            skLineSegment(sketch, "E50.19.5", {"start": v(-45.56, -16.95) * mm, "end": v(-46.49, -17.36) * mm});
            skLineSegment(sketch, "E50.19.6", {"start": v(-46.49, -17.36) * mm, "end": v(-45.25, -20.15) * mm});
            skLineSegment(sketch, "E50.19.7", {"start": v(-44, -22.93) * mm, "end": v(-45.25, -20.15) * mm});
            skLineSegment(sketch, "E50.19.8", {"start": v(-43.08, -22.52) * mm, "end": v(-44, -22.93) * mm});
            skLineSegment(sketch, "E50.19.9", {"start": v(-43.7, -21.12) * mm, "end": v(-43.08, -22.52) * mm});
            skArc(sketch, "E50.19.10", {"start": v(-43.7, -21.12) * mm, "mid": v(-43.73, -20.91) * mm, "end": v(-43.64, -20.72) * mm});
            skLineSegment(sketch, "E50.19.11", {"start": v(-43.04, -20.03) * mm, "end": v(-43.64, -20.72) * mm});
            skArc(sketch, "E50.19.12", {"start": v(-42.98, -19.62) * mm, "mid": v(-42.95, -19.83) * mm, "end": v(-43.04, -20.03) * mm});
            skLineSegment(sketch, "E50.19.13", {"start": v(-43.16, -19.22) * mm, "end": v(-42.98, -19.62) * mm});
            skLineSegment(sketch, "E50.20.0", {"start": v(-40.91, -23.62) * mm, "end": v(-41.14, -23.24) * mm});
            skArc(sketch, "E50.20.1", {"start": v(-41.14, -23.24) * mm, "mid": v(-41.3, -23.1) * mm, "end": v(-41.5, -23.05) * mm});
            skLineSegment(sketch, "E50.20.2", {"start": v(-41.5, -23.05) * mm, "end": v(-42.41, -23.13) * mm});
            skArc(sketch, "E50.20.3", {"start": v(-42.77, -22.94) * mm, "mid": v(-42.62, -23.09) * mm, "end": v(-42.41, -23.13) * mm});
            skLineSegment(sketch, "E50.20.4", {"start": v(-42.77, -22.94) * mm, "end": v(-43.54, -21.62) * mm});
            skLineSegment(sketch, "E50.20.5", {"start": v(-43.54, -21.62) * mm, "end": v(-44.42, -22.13) * mm});
            skLineSegment(sketch, "E50.20.6", {"start": v(-44.42, -22.13) * mm, "end": v(-42.9, -24.76) * mm});
            skLineSegment(sketch, "E50.20.7", {"start": v(-41.37, -27.4) * mm, "end": v(-42.9, -24.76) * mm});
            skLineSegment(sketch, "E50.20.8", {"start": v(-40.5, -26.9) * mm, "end": v(-41.37, -27.4) * mm});
            skLineSegment(sketch, "E50.20.9", {"start": v(-41.25, -25.57) * mm, "end": v(-40.5, -26.9) * mm});
            skArc(sketch, "E50.20.10", {"start": v(-41.25, -25.57) * mm, "mid": v(-41.3, -25.37) * mm, "end": v(-41.24, -25.16) * mm});
            skLineSegment(sketch, "E50.20.11", {"start": v(-40.71, -24.41) * mm, "end": v(-41.24, -25.16) * mm});
            skArc(sketch, "E50.20.12", {"start": v(-40.7, -24) * mm, "mid": v(-40.64, -24.21) * mm, "end": v(-40.71, -24.41) * mm});
            skLineSegment(sketch, "E50.20.13", {"start": v(-40.91, -23.62) * mm, "end": v(-40.7, -24) * mm});
            skLineSegment(sketch, "E50.21.0", {"start": v(-38.22, -27.77) * mm, "end": v(-38.48, -27.41) * mm});
            skArc(sketch, "E50.21.1", {"start": v(-38.48, -27.41) * mm, "mid": v(-38.65, -27.28) * mm, "end": v(-38.86, -27.26) * mm});
            skLineSegment(sketch, "E50.21.2", {"start": v(-38.86, -27.26) * mm, "end": v(-39.76, -27.44) * mm});
            skArc(sketch, "E50.21.3", {"start": v(-40.14, -27.29) * mm, "mid": v(-39.97, -27.42) * mm, "end": v(-39.76, -27.44) * mm});
            skLineSegment(sketch, "E50.21.4", {"start": v(-40.14, -27.29) * mm, "end": v(-41.04, -26.05) * mm});
            skLineSegment(sketch, "E50.21.5", {"start": v(-41.04, -26.05) * mm, "end": v(-41.86, -26.65) * mm});
            skLineSegment(sketch, "E50.21.6", {"start": v(-41.86, -26.65) * mm, "end": v(-40.07, -29.11) * mm});
            skLineSegment(sketch, "E50.21.7", {"start": v(-38.28, -31.58) * mm, "end": v(-40.07, -29.11) * mm});
            skLineSegment(sketch, "E50.21.8", {"start": v(-37.46, -30.98) * mm, "end": v(-38.28, -31.58) * mm});
            skLineSegment(sketch, "E50.21.9", {"start": v(-38.35, -29.75) * mm, "end": v(-37.46, -30.98) * mm});
            skArc(sketch, "E50.21.10", {"start": v(-38.35, -29.75) * mm, "mid": v(-38.43, -29.55) * mm, "end": v(-38.38, -29.34) * mm});
            skLineSegment(sketch, "E50.21.11", {"start": v(-37.94, -28.54) * mm, "end": v(-38.38, -29.34) * mm});
            skArc(sketch, "E50.21.12", {"start": v(-37.96, -28.13) * mm, "mid": v(-37.89, -28.33) * mm, "end": v(-37.94, -28.54) * mm});
            skLineSegment(sketch, "E50.21.13", {"start": v(-38.22, -27.77) * mm, "end": v(-37.96, -28.13) * mm});
            skLineSegment(sketch, "E50.22.0", {"start": v(-35.1, -31.61) * mm, "end": v(-35.4, -31.28) * mm});
            skArc(sketch, "E50.22.1", {"start": v(-35.4, -31.28) * mm, "mid": v(-35.59, -31.17) * mm, "end": v(-35.8, -31.17) * mm});
            skLineSegment(sketch, "E50.22.2", {"start": v(-35.8, -31.17) * mm, "end": v(-36.68, -31.44) * mm});
            skArc(sketch, "E50.22.3", {"start": v(-37.07, -31.33) * mm, "mid": v(-36.89, -31.44) * mm, "end": v(-36.68, -31.44) * mm});
            skLineSegment(sketch, "E50.22.4", {"start": v(-37.07, -31.33) * mm, "end": v(-38.1, -30.2) * mm});
            skLineSegment(sketch, "E50.22.5", {"start": v(-38.1, -30.2) * mm, "end": v(-38.85, -30.88) * mm});
            skLineSegment(sketch, "E50.22.6", {"start": v(-38.85, -30.88) * mm, "end": v(-36.8, -33.14) * mm});
            skLineSegment(sketch, "E50.22.7", {"start": v(-34.77, -35.4) * mm, "end": v(-36.8, -33.14) * mm});
            skLineSegment(sketch, "E50.22.8", {"start": v(-34.01, -34.73) * mm, "end": v(-34.77, -35.4) * mm});
            skLineSegment(sketch, "E50.22.9", {"start": v(-35.04, -33.6) * mm, "end": v(-34.01, -34.73) * mm});
            skArc(sketch, "E50.22.10", {"start": v(-35.04, -33.6) * mm, "mid": v(-35.13, -33.4) * mm, "end": v(-35.1, -33.19) * mm});
            skLineSegment(sketch, "E50.22.11", {"start": v(-34.75, -32.35) * mm, "end": v(-35.1, -33.19) * mm});
            skArc(sketch, "E50.22.12", {"start": v(-34.81, -31.94) * mm, "mid": v(-34.72, -32.13) * mm, "end": v(-34.75, -32.35) * mm});
            skLineSegment(sketch, "E50.22.13", {"start": v(-35.1, -31.61) * mm, "end": v(-34.81, -31.94) * mm});
            skLineSegment(sketch, "E50.23.0", {"start": v(-31.61, -35.1) * mm, "end": v(-31.94, -34.81) * mm});
            skArc(sketch, "E50.23.1", {"start": v(-31.94, -34.81) * mm, "mid": v(-32.13, -34.72) * mm, "end": v(-32.35, -34.75) * mm});
            skLineSegment(sketch, "E50.23.2", {"start": v(-32.35, -34.75) * mm, "end": v(-33.19, -35.1) * mm});
            skArc(sketch, "E50.23.3", {"start": v(-33.6, -35.04) * mm, "mid": v(-33.4, -35.13) * mm, "end": v(-33.19, -35.1) * mm});
            skLineSegment(sketch, "E50.23.4", {"start": v(-33.6, -35.04) * mm, "end": v(-34.73, -34.01) * mm});
            skLineSegment(sketch, "E50.23.5", {"start": v(-34.73, -34.01) * mm, "end": v(-35.4, -34.77) * mm});
            skLineSegment(sketch, "E50.23.6", {"start": v(-35.4, -34.77) * mm, "end": v(-33.14, -36.8) * mm});
            skLineSegment(sketch, "E50.23.7", {"start": v(-30.88, -38.85) * mm, "end": v(-33.14, -36.8) * mm});
            skLineSegment(sketch, "E50.23.8", {"start": v(-30.2, -38.1) * mm, "end": v(-30.88, -38.85) * mm});
            skLineSegment(sketch, "E50.23.9", {"start": v(-31.33, -37.07) * mm, "end": v(-30.2, -38.1) * mm});
            skArc(sketch, "E50.23.10", {"start": v(-31.33, -37.07) * mm, "mid": v(-31.44, -36.89) * mm, "end": v(-31.44, -36.68) * mm});
            skLineSegment(sketch, "E50.23.11", {"start": v(-31.17, -35.8) * mm, "end": v(-31.44, -36.68) * mm});
            skArc(sketch, "E50.23.12", {"start": v(-31.28, -35.4) * mm, "mid": v(-31.17, -35.59) * mm, "end": v(-31.17, -35.8) * mm});
            skLineSegment(sketch, "E50.23.13", {"start": v(-31.61, -35.1) * mm, "end": v(-31.28, -35.4) * mm});
            skLineSegment(sketch, "E50.24.0", {"start": v(-27.77, -38.22) * mm, "end": v(-28.13, -37.96) * mm});
            skArc(sketch, "E50.24.1", {"start": v(-28.13, -37.96) * mm, "mid": v(-28.33, -37.89) * mm, "end": v(-28.54, -37.94) * mm});
            skLineSegment(sketch, "E50.24.2", {"start": v(-28.54, -37.94) * mm, "end": v(-29.34, -38.38) * mm});
            skArc(sketch, "E50.24.3", {"start": v(-29.75, -38.35) * mm, "mid": v(-29.55, -38.43) * mm, "end": v(-29.34, -38.38) * mm});
            skLineSegment(sketch, "E50.24.4", {"start": v(-29.75, -38.35) * mm, "end": v(-30.98, -37.46) * mm});
            skLineSegment(sketch, "E50.24.5", {"start": v(-30.98, -37.46) * mm, "end": v(-31.58, -38.28) * mm});
            skLineSegment(sketch, "E50.24.6", {"start": v(-31.58, -38.28) * mm, "end": v(-29.11, -40.07) * mm});
            skLineSegment(sketch, "E50.24.7", {"start": v(-26.65, -41.86) * mm, "end": v(-29.11, -40.07) * mm});
            skLineSegment(sketch, "E50.24.8", {"start": v(-26.05, -41.04) * mm, "end": v(-26.65, -41.86) * mm});
            skLineSegment(sketch, "E50.24.9", {"start": v(-27.29, -40.14) * mm, "end": v(-26.05, -41.04) * mm});
            skArc(sketch, "E50.24.10", {"start": v(-27.29, -40.14) * mm, "mid": v(-27.42, -39.97) * mm, "end": v(-27.44, -39.76) * mm});
            skLineSegment(sketch, "E50.24.11", {"start": v(-27.26, -38.86) * mm, "end": v(-27.44, -39.76) * mm});
            skArc(sketch, "E50.24.12", {"start": v(-27.41, -38.48) * mm, "mid": v(-27.28, -38.65) * mm, "end": v(-27.26, -38.86) * mm});
            skLineSegment(sketch, "E50.24.13", {"start": v(-27.77, -38.22) * mm, "end": v(-27.41, -38.48) * mm});
            skLineSegment(sketch, "E50.25.0", {"start": v(-23.62, -40.91) * mm, "end": v(-24, -40.7) * mm});
            skArc(sketch, "E50.25.1", {"start": v(-24, -40.7) * mm, "mid": v(-24.21, -40.64) * mm, "end": v(-24.41, -40.71) * mm});
            skLineSegment(sketch, "E50.25.2", {"start": v(-24.41, -40.71) * mm, "end": v(-25.16, -41.24) * mm});
            skArc(sketch, "E50.25.3", {"start": v(-25.57, -41.25) * mm, "mid": v(-25.37, -41.3) * mm, "end": v(-25.16, -41.24) * mm});
            skLineSegment(sketch, "E50.25.4", {"start": v(-25.57, -41.25) * mm, "end": v(-26.9, -40.5) * mm});
            skLineSegment(sketch, "E50.25.5", {"start": v(-26.9, -40.5) * mm, "end": v(-27.4, -41.37) * mm});
            skLineSegment(sketch, "E50.25.6", {"start": v(-27.4, -41.37) * mm, "end": v(-24.77, -42.9) * mm});
            skLineSegment(sketch, "E50.25.7", {"start": v(-22.13, -44.42) * mm, "end": v(-24.76, -42.9) * mm});
            skLineSegment(sketch, "E50.25.8", {"start": v(-21.62, -43.54) * mm, "end": v(-22.13, -44.42) * mm});
            skLineSegment(sketch, "E50.25.9", {"start": v(-22.94, -42.77) * mm, "end": v(-21.62, -43.54) * mm});
            skArc(sketch, "E50.25.10", {"start": v(-22.94, -42.77) * mm, "mid": v(-23.09, -42.62) * mm, "end": v(-23.13, -42.41) * mm});
            skLineSegment(sketch, "E50.25.11", {"start": v(-23.05, -41.5) * mm, "end": v(-23.13, -42.41) * mm});
            skArc(sketch, "E50.25.12", {"start": v(-23.24, -41.14) * mm, "mid": v(-23.1, -41.3) * mm, "end": v(-23.05, -41.5) * mm});
            skLineSegment(sketch, "E50.25.13", {"start": v(-23.62, -40.91) * mm, "end": v(-23.24, -41.14) * mm});
            skLineSegment(sketch, "E50.26.0", {"start": v(-19.22, -43.16) * mm, "end": v(-19.62, -42.98) * mm});
            skArc(sketch, "E50.26.1", {"start": v(-19.62, -42.98) * mm, "mid": v(-19.83, -42.95) * mm, "end": v(-20.03, -43.04) * mm});
            skLineSegment(sketch, "E50.26.2", {"start": v(-20.03, -43.04) * mm, "end": v(-20.72, -43.64) * mm});
            skArc(sketch, "E50.26.3", {"start": v(-21.12, -43.7) * mm, "mid": v(-20.91, -43.73) * mm, "end": v(-20.72, -43.64) * mm});
            skLineSegment(sketch, "E50.26.4", {"start": v(-21.12, -43.7) * mm, "end": v(-22.52, -43.08) * mm});
            skLineSegment(sketch, "E50.26.5", {"start": v(-22.52, -43.08) * mm, "end": v(-22.93, -44) * mm});
            skLineSegment(sketch, "E50.26.6", {"start": v(-22.93, -44) * mm, "end": v(-20.15, -45.25) * mm});
            skLineSegment(sketch, "E50.26.7", {"start": v(-17.36, -46.49) * mm, "end": v(-20.15, -45.25) * mm});
            skLineSegment(sketch, "E50.26.8", {"start": v(-16.95, -45.56) * mm, "end": v(-17.36, -46.49) * mm});
            skLineSegment(sketch, "E50.26.9", {"start": v(-18.34, -44.94) * mm, "end": v(-16.95, -45.56) * mm});
            skArc(sketch, "E50.26.10", {"start": v(-18.34, -44.94) * mm, "mid": v(-18.5, -44.8) * mm, "end": v(-18.57, -44.6) * mm});
            skLineSegment(sketch, "E50.26.11", {"start": v(-18.59, -43.68) * mm, "end": v(-18.57, -44.6) * mm});
            skArc(sketch, "E50.26.12", {"start": v(-18.81, -43.34) * mm, "mid": v(-18.65, -43.48) * mm, "end": v(-18.59, -43.68) * mm});
            skLineSegment(sketch, "E50.26.13", {"start": v(-19.22, -43.16) * mm, "end": v(-18.81, -43.34) * mm});
            skLineSegment(sketch, "E50.27.0", {"start": v(-14.6, -44.93) * mm, "end": v(-15.02, -44.8) * mm});
            skArc(sketch, "E50.27.1", {"start": v(-15.02, -44.8) * mm, "mid": v(-15.23, -44.79) * mm, "end": v(-15.42, -44.9) * mm});
            skLineSegment(sketch, "E50.27.2", {"start": v(-15.42, -44.9) * mm, "end": v(-16.04, -45.57) * mm});
            skArc(sketch, "E50.27.3", {"start": v(-16.44, -45.67) * mm, "mid": v(-16.22, -45.68) * mm, "end": v(-16.04, -45.57) * mm});
            skLineSegment(sketch, "E50.27.4", {"start": v(-16.44, -45.67) * mm, "end": v(-17.9, -45.2) * mm});
            skLineSegment(sketch, "E50.27.5", {"start": v(-17.9, -45.2) * mm, "end": v(-18.2, -46.16) * mm});
            skLineSegment(sketch, "E50.27.6", {"start": v(-18.2, -46.16) * mm, "end": v(-15.3, -47.1) * mm});
            skLineSegment(sketch, "E50.27.7", {"start": v(-12.4, -48.05) * mm, "end": v(-15.3, -47.1) * mm});
            skLineSegment(sketch, "E50.27.8", {"start": v(-12.1, -47.08) * mm, "end": v(-12.4, -48.05) * mm});
            skLineSegment(sketch, "E50.27.9", {"start": v(-13.55, -46.6) * mm, "end": v(-12.1, -47.08) * mm});
            skArc(sketch, "E50.27.10", {"start": v(-13.55, -46.6) * mm, "mid": v(-13.72, -46.49) * mm, "end": v(-13.8, -46.3) * mm});
            skLineSegment(sketch, "E50.27.11", {"start": v(-13.92, -45.38) * mm, "end": v(-13.8, -46.3) * mm});
            skArc(sketch, "E50.27.12", {"start": v(-14.18, -45.07) * mm, "mid": v(-14, -45.19) * mm, "end": v(-13.92, -45.38) * mm});
            skLineSegment(sketch, "E50.27.13", {"start": v(-14.6, -44.93) * mm, "end": v(-14.18, -45.07) * mm});
            skLineSegment(sketch, "E50.28.0", {"start": v(-9.82, -46.21) * mm, "end": v(-10.26, -46.12) * mm});
            skArc(sketch, "E50.28.1", {"start": v(-10.26, -46.12) * mm, "mid": v(-10.47, -46.14) * mm, "end": v(-10.64, -46.26) * mm});
            skLineSegment(sketch, "E50.28.2", {"start": v(-10.64, -46.26) * mm, "end": v(-11.2, -47) * mm});
            skArc(sketch, "E50.28.3", {"start": v(-11.57, -47.14) * mm, "mid": v(-11.36, -47.12) * mm, "end": v(-11.2, -47) * mm});
            skLineSegment(sketch, "E50.28.4", {"start": v(-11.57, -47.14) * mm, "end": v(-13.07, -46.82) * mm});
            skLineSegment(sketch, "E50.28.5", {"start": v(-13.07, -46.82) * mm, "end": v(-13.28, -47.81) * mm});
            skLineSegment(sketch, "E50.28.6", {"start": v(-13.28, -47.81) * mm, "end": v(-10.3, -48.45) * mm});
            skLineSegment(sketch, "E50.28.7", {"start": v(-7.32, -49.08) * mm, "end": v(-10.3, -48.45) * mm});
            skLineSegment(sketch, "E50.28.8", {"start": v(-7.1, -48.09) * mm, "end": v(-7.32, -49.08) * mm});
            skLineSegment(sketch, "E50.28.9", {"start": v(-8.6, -47.77) * mm, "end": v(-7.1, -48.09) * mm});
            skArc(sketch, "E50.28.10", {"start": v(-8.6, -47.77) * mm, "mid": v(-8.79, -47.67) * mm, "end": v(-8.9, -47.48) * mm});
            skLineSegment(sketch, "E50.28.11", {"start": v(-9.1, -46.6) * mm, "end": v(-8.9, -47.48) * mm});
            skArc(sketch, "E50.28.12", {"start": v(-9.39, -46.3) * mm, "mid": v(-9.2, -46.4) * mm, "end": v(-9.1, -46.6) * mm});
            skLineSegment(sketch, "E50.28.13", {"start": v(-9.82, -46.21) * mm, "end": v(-9.39, -46.3) * mm});
            skLineSegment(sketch, "E50.29.0", {"start": v(-4.94, -46.99) * mm, "end": v(-5.38, -46.94) * mm});
            skArc(sketch, "E50.29.1", {"start": v(-5.38, -46.94) * mm, "mid": v(-5.59, -46.98) * mm, "end": v(-5.75, -47.12) * mm});
            skLineSegment(sketch, "E50.29.2", {"start": v(-5.75, -47.12) * mm, "end": v(-6.22, -47.9) * mm});
            skArc(sketch, "E50.29.3", {"start": v(-6.58, -48.09) * mm, "mid": v(-6.37, -48.05) * mm, "end": v(-6.22, -47.9) * mm});
            skLineSegment(sketch, "E50.29.4", {"start": v(-6.58, -48.09) * mm, "end": v(-8.1, -47.93) * mm});
            skLineSegment(sketch, "E50.29.5", {"start": v(-8.1, -47.93) * mm, "end": v(-8.2, -48.94) * mm});
            skLineSegment(sketch, "E50.29.6", {"start": v(-8.2, -48.94) * mm, "end": v(-5.18, -49.26) * mm});
            skLineSegment(sketch, "E50.29.7", {"start": v(-2.15, -49.58) * mm, "end": v(-5.18, -49.26) * mm});
            skLineSegment(sketch, "E50.29.8", {"start": v(-2.04, -48.57) * mm, "end": v(-2.15, -49.58) * mm});
            skLineSegment(sketch, "E50.29.9", {"start": v(-3.56, -48.4) * mm, "end": v(-2.04, -48.57) * mm});
            skArc(sketch, "E50.29.10", {"start": v(-3.56, -48.4) * mm, "mid": v(-3.76, -48.33) * mm, "end": v(-3.88, -48.15) * mm});
            skLineSegment(sketch, "E50.29.11", {"start": v(-4.18, -47.29) * mm, "end": v(-3.88, -48.15) * mm});
            skArc(sketch, "E50.29.12", {"start": v(-4.5, -47.03) * mm, "mid": v(-4.3, -47.11) * mm, "end": v(-4.18, -47.29) * mm});
            skLineSegment(sketch, "E50.29.13", {"start": v(-4.94, -46.99) * mm, "end": v(-4.5, -47.03) * mm});
            skLineSegment(sketch, "E50.30.0", {"start": v(0, -47.24) * mm, "end": v(-0.44, -47.24) * mm});
            skArc(sketch, "E50.30.1", {"start": v(-0.44, -47.24) * mm, "mid": v(-0.65, -47.3) * mm, "end": v(-0.79, -47.46) * mm});
            skLineSegment(sketch, "E50.30.2", {"start": v(-0.79, -47.46) * mm, "end": v(-1.18, -48.3) * mm});
            skArc(sketch, "E50.30.3", {"start": v(-1.52, -48.51) * mm, "mid": v(-1.32, -48.45) * mm, "end": v(-1.18, -48.3) * mm});
            skLineSegment(sketch, "E50.30.4", {"start": v(-1.52, -48.51) * mm, "end": v(-3.05, -48.51) * mm});
            skLineSegment(sketch, "E50.30.5", {"start": v(-3.05, -48.51) * mm, "end": v(-3.05, -49.53) * mm});
            skLineSegment(sketch, "E50.30.6", {"start": v(-3.05, -49.53) * mm, "end": v(0, -49.53) * mm});
            skLineSegment(sketch, "E50.30.7", {"start": v(3.05, -49.53) * mm, "end": v(0, -49.53) * mm});
            skLineSegment(sketch, "E50.30.8", {"start": v(3.05, -48.51) * mm, "end": v(3.05, -49.53) * mm});
            skLineSegment(sketch, "E50.30.9", {"start": v(1.52, -48.51) * mm, "end": v(3.05, -48.51) * mm});
            skArc(sketch, "E50.30.10", {"start": v(1.52, -48.51) * mm, "mid": v(1.32, -48.45) * mm, "end": v(1.18, -48.3) * mm});
            skLineSegment(sketch, "E50.30.11", {"start": v(0.79, -47.46) * mm, "end": v(1.18, -48.3) * mm});
            skArc(sketch, "E50.30.12", {"start": v(0.44, -47.24) * mm, "mid": v(0.65, -47.3) * mm, "end": v(0.79, -47.46) * mm});
            skLineSegment(sketch, "E50.30.13", {"start": v(0, -47.24) * mm, "end": v(0.44, -47.24) * mm});
            skLineSegment(sketch, "E50.31.0", {"start": v(4.94, -46.99) * mm, "end": v(4.5, -47.03) * mm});
            skArc(sketch, "E50.31.1", {"start": v(4.5, -47.03) * mm, "mid": v(4.3, -47.11) * mm, "end": v(4.18, -47.29) * mm});
            skLineSegment(sketch, "E50.31.2", {"start": v(4.18, -47.29) * mm, "end": v(3.88, -48.15) * mm});
            skArc(sketch, "E50.31.3", {"start": v(3.56, -48.4) * mm, "mid": v(3.76, -48.33) * mm, "end": v(3.88, -48.15) * mm});
            skLineSegment(sketch, "E50.31.4", {"start": v(3.56, -48.4) * mm, "end": v(2.04, -48.57) * mm});
            skLineSegment(sketch, "E50.31.5", {"start": v(2.04, -48.57) * mm, "end": v(2.15, -49.58) * mm});
            skLineSegment(sketch, "E50.31.6", {"start": v(2.15, -49.58) * mm, "end": v(5.18, -49.26) * mm});
            skLineSegment(sketch, "E50.31.7", {"start": v(8.2, -48.94) * mm, "end": v(5.18, -49.26) * mm});
            skLineSegment(sketch, "E50.31.8", {"start": v(8.1, -47.93) * mm, "end": v(8.2, -48.94) * mm});
            skLineSegment(sketch, "E50.31.9", {"start": v(6.58, -48.09) * mm, "end": v(8.1, -47.93) * mm});
            skArc(sketch, "E50.31.10", {"start": v(6.58, -48.09) * mm, "mid": v(6.37, -48.05) * mm, "end": v(6.22, -47.9) * mm});
            skLineSegment(sketch, "E50.31.11", {"start": v(5.75, -47.12) * mm, "end": v(6.22, -47.9) * mm});
            skArc(sketch, "E50.31.12", {"start": v(5.38, -46.94) * mm, "mid": v(5.59, -46.98) * mm, "end": v(5.75, -47.12) * mm});
            skLineSegment(sketch, "E50.31.13", {"start": v(4.94, -46.99) * mm, "end": v(5.38, -46.94) * mm});
            skLineSegment(sketch, "E50.32.0", {"start": v(9.82, -46.21) * mm, "end": v(9.39, -46.3) * mm});
            skArc(sketch, "E50.32.1", {"start": v(9.39, -46.3) * mm, "mid": v(9.2, -46.4) * mm, "end": v(9.1, -46.6) * mm});
            skLineSegment(sketch, "E50.32.2", {"start": v(9.1, -46.6) * mm, "end": v(8.9, -47.48) * mm});
            skArc(sketch, "E50.32.3", {"start": v(8.6, -47.77) * mm, "mid": v(8.79, -47.67) * mm, "end": v(8.9, -47.48) * mm});
            skLineSegment(sketch, "E50.32.4", {"start": v(8.6, -47.77) * mm, "end": v(7.1, -48.09) * mm});
            skLineSegment(sketch, "E50.32.5", {"start": v(7.1, -48.09) * mm, "end": v(7.32, -49.08) * mm});
            skLineSegment(sketch, "E50.32.6", {"start": v(7.32, -49.08) * mm, "end": v(10.3, -48.45) * mm});
            skLineSegment(sketch, "E50.32.7", {"start": v(13.28, -47.81) * mm, "end": v(10.3, -48.45) * mm});
            skLineSegment(sketch, "E50.32.8", {"start": v(13.07, -46.82) * mm, "end": v(13.28, -47.81) * mm});
            skLineSegment(sketch, "E50.32.9", {"start": v(11.57, -47.14) * mm, "end": v(13.07, -46.82) * mm});
            skArc(sketch, "E50.32.10", {"start": v(11.57, -47.14) * mm, "mid": v(11.36, -47.12) * mm, "end": v(11.2, -47) * mm});
            skLineSegment(sketch, "E50.32.11", {"start": v(10.64, -46.26) * mm, "end": v(11.2, -47) * mm});
            skArc(sketch, "E50.32.12", {"start": v(10.26, -46.12) * mm, "mid": v(10.47, -46.14) * mm, "end": v(10.64, -46.26) * mm});
            skLineSegment(sketch, "E50.32.13", {"start": v(9.82, -46.21) * mm, "end": v(10.26, -46.12) * mm});
            skLineSegment(sketch, "E50.33.0", {"start": v(14.6, -44.93) * mm, "end": v(14.18, -45.07) * mm});
            skArc(sketch, "E50.33.1", {"start": v(14.18, -45.07) * mm, "mid": v(14, -45.19) * mm, "end": v(13.92, -45.38) * mm});
            skLineSegment(sketch, "E50.33.2", {"start": v(13.92, -45.38) * mm, "end": v(13.8, -46.3) * mm});
            skArc(sketch, "E50.33.3", {"start": v(13.55, -46.6) * mm, "mid": v(13.72, -46.49) * mm, "end": v(13.8, -46.3) * mm});
            skLineSegment(sketch, "E50.33.4", {"start": v(13.55, -46.6) * mm, "end": v(12.1, -47.08) * mm});
            skLineSegment(sketch, "E50.33.5", {"start": v(12.1, -47.08) * mm, "end": v(12.4, -48.05) * mm});
            skLineSegment(sketch, "E50.33.6", {"start": v(12.4, -48.05) * mm, "end": v(15.3, -47.1) * mm});
            skLineSegment(sketch, "E50.33.7", {"start": v(18.2, -46.16) * mm, "end": v(15.3, -47.1) * mm});
            skLineSegment(sketch, "E50.33.8", {"start": v(17.9, -45.2) * mm, "end": v(18.2, -46.16) * mm});
            skLineSegment(sketch, "E50.33.9", {"start": v(16.44, -45.67) * mm, "end": v(17.9, -45.2) * mm});
            skArc(sketch, "E50.33.10", {"start": v(16.44, -45.67) * mm, "mid": v(16.22, -45.68) * mm, "end": v(16.04, -45.57) * mm});
            skLineSegment(sketch, "E50.33.11", {"start": v(15.42, -44.9) * mm, "end": v(16.04, -45.57) * mm});
            skArc(sketch, "E50.33.12", {"start": v(15.02, -44.8) * mm, "mid": v(15.23, -44.79) * mm, "end": v(15.42, -44.9) * mm});
            skLineSegment(sketch, "E50.33.13", {"start": v(14.6, -44.93) * mm, "end": v(15.02, -44.8) * mm});
            skLineSegment(sketch, "E50.34.0", {"start": v(19.22, -43.16) * mm, "end": v(18.81, -43.34) * mm});
            skArc(sketch, "E50.34.1", {"start": v(18.81, -43.34) * mm, "mid": v(18.65, -43.48) * mm, "end": v(18.59, -43.68) * mm});
            skLineSegment(sketch, "E50.34.2", {"start": v(18.59, -43.68) * mm, "end": v(18.57, -44.6) * mm});
            skArc(sketch, "E50.34.3", {"start": v(18.34, -44.94) * mm, "mid": v(18.5, -44.8) * mm, "end": v(18.57, -44.6) * mm});
            skLineSegment(sketch, "E50.34.4", {"start": v(18.34, -44.94) * mm, "end": v(16.95, -45.56) * mm});
            skLineSegment(sketch, "E50.34.5", {"start": v(16.95, -45.56) * mm, "end": v(17.36, -46.49) * mm});
            skLineSegment(sketch, "E50.34.6", {"start": v(17.36, -46.49) * mm, "end": v(20.15, -45.25) * mm});
            skLineSegment(sketch, "E50.34.7", {"start": v(22.93, -44) * mm, "end": v(20.15, -45.25) * mm});
            skLineSegment(sketch, "E50.34.8", {"start": v(22.52, -43.08) * mm, "end": v(22.93, -44) * mm});
            skLineSegment(sketch, "E50.34.9", {"start": v(21.12, -43.7) * mm, "end": v(22.52, -43.08) * mm});
            skArc(sketch, "E50.34.10", {"start": v(21.12, -43.7) * mm, "mid": v(20.91, -43.73) * mm, "end": v(20.72, -43.64) * mm});
            skLineSegment(sketch, "E50.34.11", {"start": v(20.03, -43.04) * mm, "end": v(20.72, -43.64) * mm});
            skArc(sketch, "E50.34.12", {"start": v(19.62, -42.98) * mm, "mid": v(19.83, -42.95) * mm, "end": v(20.03, -43.04) * mm});
            skLineSegment(sketch, "E50.34.13", {"start": v(19.22, -43.16) * mm, "end": v(19.62, -42.98) * mm});
            skLineSegment(sketch, "E50.35.0", {"start": v(23.62, -40.91) * mm, "end": v(23.24, -41.14) * mm});
            skArc(sketch, "E50.35.1", {"start": v(23.24, -41.14) * mm, "mid": v(23.1, -41.3) * mm, "end": v(23.05, -41.5) * mm});
            skLineSegment(sketch, "E50.35.2", {"start": v(23.05, -41.5) * mm, "end": v(23.13, -42.41) * mm});
            skArc(sketch, "E50.35.3", {"start": v(22.94, -42.77) * mm, "mid": v(23.09, -42.62) * mm, "end": v(23.13, -42.41) * mm});
            skLineSegment(sketch, "E50.35.4", {"start": v(22.94, -42.77) * mm, "end": v(21.62, -43.54) * mm});
            skLineSegment(sketch, "E50.35.5", {"start": v(21.62, -43.54) * mm, "end": v(22.13, -44.42) * mm});
            skLineSegment(sketch, "E50.35.6", {"start": v(22.13, -44.42) * mm, "end": v(24.76, -42.9) * mm});
            skLineSegment(sketch, "E50.35.7", {"start": v(27.4, -41.37) * mm, "end": v(24.76, -42.9) * mm});
            skLineSegment(sketch, "E50.35.8", {"start": v(26.9, -40.5) * mm, "end": v(27.4, -41.37) * mm});
            skLineSegment(sketch, "E50.35.9", {"start": v(25.57, -41.25) * mm, "end": v(26.9, -40.5) * mm});
            skArc(sketch, "E50.35.10", {"start": v(25.57, -41.25) * mm, "mid": v(25.37, -41.3) * mm, "end": v(25.16, -41.24) * mm});
            skLineSegment(sketch, "E50.35.11", {"start": v(24.41, -40.71) * mm, "end": v(25.16, -41.24) * mm});
            skArc(sketch, "E50.35.12", {"start": v(24, -40.7) * mm, "mid": v(24.21, -40.64) * mm, "end": v(24.41, -40.71) * mm});
            skLineSegment(sketch, "E50.35.13", {"start": v(23.62, -40.91) * mm, "end": v(24, -40.7) * mm});
            skLineSegment(sketch, "E50.36.0", {"start": v(27.77, -38.22) * mm, "end": v(27.41, -38.48) * mm});
            skArc(sketch, "E50.36.1", {"start": v(27.41, -38.48) * mm, "mid": v(27.28, -38.65) * mm, "end": v(27.26, -38.86) * mm});
            skLineSegment(sketch, "E50.36.2", {"start": v(27.26, -38.86) * mm, "end": v(27.44, -39.76) * mm});
            skArc(sketch, "E50.36.3", {"start": v(27.29, -40.14) * mm, "mid": v(27.42, -39.97) * mm, "end": v(27.44, -39.76) * mm});
            skLineSegment(sketch, "E50.36.4", {"start": v(27.29, -40.14) * mm, "end": v(26.05, -41.04) * mm});
            skLineSegment(sketch, "E50.36.5", {"start": v(26.05, -41.04) * mm, "end": v(26.65, -41.86) * mm});
            skLineSegment(sketch, "E50.36.6", {"start": v(26.65, -41.86) * mm, "end": v(29.11, -40.07) * mm});
            skLineSegment(sketch, "E50.36.7", {"start": v(31.58, -38.28) * mm, "end": v(29.11, -40.07) * mm});
            skLineSegment(sketch, "E50.36.8", {"start": v(30.98, -37.46) * mm, "end": v(31.58, -38.28) * mm});
            skLineSegment(sketch, "E50.36.9", {"start": v(29.75, -38.35) * mm, "end": v(30.98, -37.46) * mm});
            skArc(sketch, "E50.36.10", {"start": v(29.75, -38.35) * mm, "mid": v(29.55, -38.43) * mm, "end": v(29.34, -38.38) * mm});
            skLineSegment(sketch, "E50.36.11", {"start": v(28.54, -37.94) * mm, "end": v(29.34, -38.38) * mm});
            skArc(sketch, "E50.36.12", {"start": v(28.13, -37.96) * mm, "mid": v(28.33, -37.89) * mm, "end": v(28.54, -37.94) * mm});
            skLineSegment(sketch, "E50.36.13", {"start": v(27.77, -38.22) * mm, "end": v(28.13, -37.96) * mm});
            skLineSegment(sketch, "E50.37.0", {"start": v(31.61, -35.1) * mm, "end": v(31.28, -35.4) * mm});
            skArc(sketch, "E50.37.1", {"start": v(31.28, -35.4) * mm, "mid": v(31.17, -35.59) * mm, "end": v(31.17, -35.8) * mm});
            skLineSegment(sketch, "E50.37.2", {"start": v(31.17, -35.8) * mm, "end": v(31.44, -36.68) * mm});
            skArc(sketch, "E50.37.3", {"start": v(31.33, -37.07) * mm, "mid": v(31.44, -36.89) * mm, "end": v(31.44, -36.68) * mm});
            skLineSegment(sketch, "E50.37.4", {"start": v(31.33, -37.07) * mm, "end": v(30.2, -38.1) * mm});
            skLineSegment(sketch, "E50.37.5", {"start": v(30.2, -38.1) * mm, "end": v(30.88, -38.85) * mm});
            skLineSegment(sketch, "E50.37.6", {"start": v(30.88, -38.85) * mm, "end": v(33.14, -36.8) * mm});
            skLineSegment(sketch, "E50.37.7", {"start": v(35.4, -34.77) * mm, "end": v(33.14, -36.8) * mm});
            skLineSegment(sketch, "E50.37.8", {"start": v(34.73, -34.01) * mm, "end": v(35.4, -34.77) * mm});
            skLineSegment(sketch, "E50.37.9", {"start": v(33.6, -35.04) * mm, "end": v(34.73, -34.01) * mm});
            skArc(sketch, "E50.37.10", {"start": v(33.6, -35.04) * mm, "mid": v(33.4, -35.13) * mm, "end": v(33.19, -35.1) * mm});
            skLineSegment(sketch, "E50.37.11", {"start": v(32.35, -34.75) * mm, "end": v(33.19, -35.1) * mm});
            skArc(sketch, "E50.37.12", {"start": v(31.94, -34.81) * mm, "mid": v(32.13, -34.72) * mm, "end": v(32.35, -34.75) * mm});
            skLineSegment(sketch, "E50.37.13", {"start": v(31.61, -35.1) * mm, "end": v(31.94, -34.81) * mm});
            skLineSegment(sketch, "E50.38.0", {"start": v(35.1, -31.61) * mm, "end": v(34.81, -31.94) * mm});
            skArc(sketch, "E50.38.1", {"start": v(34.81, -31.94) * mm, "mid": v(34.72, -32.13) * mm, "end": v(34.75, -32.35) * mm});
            skLineSegment(sketch, "E50.38.2", {"start": v(34.75, -32.35) * mm, "end": v(35.1, -33.19) * mm});
            skArc(sketch, "E50.38.3", {"start": v(35.04, -33.6) * mm, "mid": v(35.13, -33.4) * mm, "end": v(35.1, -33.19) * mm});
            skLineSegment(sketch, "E50.38.4", {"start": v(35.04, -33.6) * mm, "end": v(34.01, -34.73) * mm});
            skLineSegment(sketch, "E50.38.5", {"start": v(34.01, -34.73) * mm, "end": v(34.77, -35.4) * mm});
            skLineSegment(sketch, "E50.38.6", {"start": v(34.77, -35.4) * mm, "end": v(36.8, -33.14) * mm});
            skLineSegment(sketch, "E50.38.7", {"start": v(38.85, -30.88) * mm, "end": v(36.8, -33.14) * mm});
            skLineSegment(sketch, "E50.38.8", {"start": v(38.1, -30.2) * mm, "end": v(38.85, -30.88) * mm});
            skLineSegment(sketch, "E50.38.9", {"start": v(37.07, -31.33) * mm, "end": v(38.1, -30.2) * mm});
            skArc(sketch, "E50.38.10", {"start": v(37.07, -31.33) * mm, "mid": v(36.89, -31.44) * mm, "end": v(36.68, -31.44) * mm});
            skLineSegment(sketch, "E50.38.11", {"start": v(35.8, -31.17) * mm, "end": v(36.68, -31.44) * mm});
            skArc(sketch, "E50.38.12", {"start": v(35.4, -31.28) * mm, "mid": v(35.59, -31.17) * mm, "end": v(35.8, -31.17) * mm});
            skLineSegment(sketch, "E50.38.13", {"start": v(35.1, -31.61) * mm, "end": v(35.4, -31.28) * mm});
            skLineSegment(sketch, "E50.39.0", {"start": v(38.22, -27.77) * mm, "end": v(37.96, -28.13) * mm});
            skArc(sketch, "E50.39.1", {"start": v(37.96, -28.13) * mm, "mid": v(37.89, -28.33) * mm, "end": v(37.94, -28.54) * mm});
            skLineSegment(sketch, "E50.39.2", {"start": v(37.94, -28.54) * mm, "end": v(38.38, -29.34) * mm});
            skArc(sketch, "E50.39.3", {"start": v(38.35, -29.75) * mm, "mid": v(38.43, -29.55) * mm, "end": v(38.38, -29.34) * mm});
            skLineSegment(sketch, "E50.39.4", {"start": v(38.35, -29.75) * mm, "end": v(37.46, -30.98) * mm});
            skLineSegment(sketch, "E50.39.5", {"start": v(37.46, -30.98) * mm, "end": v(38.28, -31.58) * mm});
            skLineSegment(sketch, "E50.39.6", {"start": v(38.28, -31.58) * mm, "end": v(40.07, -29.11) * mm});
            skLineSegment(sketch, "E50.39.7", {"start": v(41.86, -26.65) * mm, "end": v(40.07, -29.11) * mm});
            skLineSegment(sketch, "E50.39.8", {"start": v(41.04, -26.05) * mm, "end": v(41.86, -26.65) * mm});
            skLineSegment(sketch, "E50.39.9", {"start": v(40.14, -27.29) * mm, "end": v(41.04, -26.05) * mm});
            skArc(sketch, "E50.39.10", {"start": v(40.14, -27.29) * mm, "mid": v(39.97, -27.42) * mm, "end": v(39.76, -27.44) * mm});
            skLineSegment(sketch, "E50.39.11", {"start": v(38.86, -27.26) * mm, "end": v(39.76, -27.44) * mm});
            skArc(sketch, "E50.39.12", {"start": v(38.48, -27.41) * mm, "mid": v(38.65, -27.28) * mm, "end": v(38.86, -27.26) * mm});
            skLineSegment(sketch, "E50.39.13", {"start": v(38.22, -27.77) * mm, "end": v(38.48, -27.41) * mm});
            skLineSegment(sketch, "E50.40.0", {"start": v(40.91, -23.62) * mm, "end": v(40.7, -24) * mm});
            skArc(sketch, "E50.40.1", {"start": v(40.7, -24) * mm, "mid": v(40.64, -24.21) * mm, "end": v(40.71, -24.41) * mm});
            skLineSegment(sketch, "E50.40.2", {"start": v(40.71, -24.41) * mm, "end": v(41.24, -25.16) * mm});
            skArc(sketch, "E50.40.3", {"start": v(41.25, -25.57) * mm, "mid": v(41.3, -25.37) * mm, "end": v(41.24, -25.16) * mm});
            skLineSegment(sketch, "E50.40.4", {"start": v(41.25, -25.57) * mm, "end": v(40.5, -26.9) * mm});
            skLineSegment(sketch, "E50.40.5", {"start": v(40.5, -26.9) * mm, "end": v(41.37, -27.4) * mm});
            skLineSegment(sketch, "E50.40.6", {"start": v(41.37, -27.4) * mm, "end": v(42.9, -24.77) * mm});
            skLineSegment(sketch, "E50.40.7", {"start": v(44.42, -22.13) * mm, "end": v(42.9, -24.77) * mm});
            skLineSegment(sketch, "E50.40.8", {"start": v(43.54, -21.62) * mm, "end": v(44.42, -22.13) * mm});
            skLineSegment(sketch, "E50.40.9", {"start": v(42.77, -22.94) * mm, "end": v(43.54, -21.62) * mm});
            skArc(sketch, "E50.40.10", {"start": v(42.77, -22.94) * mm, "mid": v(42.62, -23.09) * mm, "end": v(42.41, -23.13) * mm});
            skLineSegment(sketch, "E50.40.11", {"start": v(41.5, -23.05) * mm, "end": v(42.41, -23.13) * mm});
            skArc(sketch, "E50.40.12", {"start": v(41.14, -23.24) * mm, "mid": v(41.3, -23.1) * mm, "end": v(41.5, -23.05) * mm});
            skLineSegment(sketch, "E50.40.13", {"start": v(40.91, -23.62) * mm, "end": v(41.14, -23.24) * mm});
            skLineSegment(sketch, "E50.41.0", {"start": v(43.16, -19.22) * mm, "end": v(42.98, -19.62) * mm});
            skArc(sketch, "E50.41.1", {"start": v(42.98, -19.62) * mm, "mid": v(42.95, -19.83) * mm, "end": v(43.04, -20.03) * mm});
            skLineSegment(sketch, "E50.41.2", {"start": v(43.04, -20.03) * mm, "end": v(43.64, -20.72) * mm});
            skArc(sketch, "E50.41.3", {"start": v(43.7, -21.12) * mm, "mid": v(43.73, -20.91) * mm, "end": v(43.64, -20.72) * mm});
            skLineSegment(sketch, "E50.41.4", {"start": v(43.7, -21.12) * mm, "end": v(43.08, -22.52) * mm});
            skLineSegment(sketch, "E50.41.5", {"start": v(43.08, -22.52) * mm, "end": v(44, -22.93) * mm});
            skLineSegment(sketch, "E50.41.6", {"start": v(44, -22.93) * mm, "end": v(45.25, -20.15) * mm});
            skLineSegment(sketch, "E50.41.7", {"start": v(46.49, -17.36) * mm, "end": v(45.25, -20.15) * mm});
            skLineSegment(sketch, "E50.41.8", {"start": v(45.56, -16.95) * mm, "end": v(46.49, -17.36) * mm});
            skLineSegment(sketch, "E50.41.9", {"start": v(44.94, -18.34) * mm, "end": v(45.56, -16.95) * mm});
            skArc(sketch, "E50.41.10", {"start": v(44.94, -18.34) * mm, "mid": v(44.8, -18.5) * mm, "end": v(44.6, -18.57) * mm});
            skLineSegment(sketch, "E50.41.11", {"start": v(43.68, -18.59) * mm, "end": v(44.6, -18.57) * mm});
            skArc(sketch, "E50.41.12", {"start": v(43.34, -18.81) * mm, "mid": v(43.48, -18.65) * mm, "end": v(43.68, -18.59) * mm});
            skLineSegment(sketch, "E50.41.13", {"start": v(43.16, -19.22) * mm, "end": v(43.34, -18.81) * mm});
            skLineSegment(sketch, "E50.42.0", {"start": v(44.93, -14.6) * mm, "end": v(44.8, -15.02) * mm});
            skArc(sketch, "E50.42.1", {"start": v(44.8, -15.02) * mm, "mid": v(44.79, -15.23) * mm, "end": v(44.9, -15.42) * mm});
            skLineSegment(sketch, "E50.42.2", {"start": v(44.9, -15.42) * mm, "end": v(45.57, -16.04) * mm});
            skArc(sketch, "E50.42.3", {"start": v(45.67, -16.44) * mm, "mid": v(45.68, -16.22) * mm, "end": v(45.57, -16.04) * mm});
            skLineSegment(sketch, "E50.42.4", {"start": v(45.67, -16.44) * mm, "end": v(45.2, -17.9) * mm});
            skLineSegment(sketch, "E50.42.5", {"start": v(45.2, -17.9) * mm, "end": v(46.16, -18.2) * mm});
            skLineSegment(sketch, "E50.42.6", {"start": v(46.16, -18.2) * mm, "end": v(47.1, -15.3) * mm});
            skLineSegment(sketch, "E50.42.7", {"start": v(48.05, -12.4) * mm, "end": v(47.1, -15.3) * mm});
            skLineSegment(sketch, "E50.42.8", {"start": v(47.08, -12.1) * mm, "end": v(48.05, -12.4) * mm});
            skLineSegment(sketch, "E50.42.9", {"start": v(46.6, -13.55) * mm, "end": v(47.08, -12.1) * mm});
            skArc(sketch, "E50.42.10", {"start": v(46.6, -13.55) * mm, "mid": v(46.49, -13.72) * mm, "end": v(46.3, -13.8) * mm});
            skLineSegment(sketch, "E50.42.11", {"start": v(45.38, -13.92) * mm, "end": v(46.3, -13.8) * mm});
            skArc(sketch, "E50.42.12", {"start": v(45.07, -14.18) * mm, "mid": v(45.19, -14) * mm, "end": v(45.38, -13.92) * mm});
            skLineSegment(sketch, "E50.42.13", {"start": v(44.93, -14.6) * mm, "end": v(45.07, -14.18) * mm});
            skLineSegment(sketch, "E50.43.0", {"start": v(46.21, -9.82) * mm, "end": v(46.12, -10.26) * mm});
            skArc(sketch, "E50.43.1", {"start": v(46.12, -10.26) * mm, "mid": v(46.14, -10.47) * mm, "end": v(46.26, -10.64) * mm});
            skLineSegment(sketch, "E50.43.2", {"start": v(46.26, -10.64) * mm, "end": v(47, -11.2) * mm});
            skArc(sketch, "E50.43.3", {"start": v(47.14, -11.57) * mm, "mid": v(47.12, -11.36) * mm, "end": v(47, -11.2) * mm});
            skLineSegment(sketch, "E50.43.4", {"start": v(47.14, -11.57) * mm, "end": v(46.82, -13.07) * mm});
            skLineSegment(sketch, "E50.43.5", {"start": v(46.82, -13.07) * mm, "end": v(47.81, -13.28) * mm});
            skLineSegment(sketch, "E50.43.6", {"start": v(47.81, -13.28) * mm, "end": v(48.45, -10.3) * mm});
            skLineSegment(sketch, "E50.43.7", {"start": v(49.08, -7.32) * mm, "end": v(48.45, -10.3) * mm});
            skLineSegment(sketch, "E50.43.8", {"start": v(48.09, -7.1) * mm, "end": v(49.08, -7.32) * mm});
            skLineSegment(sketch, "E50.43.9", {"start": v(47.77, -8.6) * mm, "end": v(48.09, -7.1) * mm});
            skArc(sketch, "E50.43.10", {"start": v(47.77, -8.6) * mm, "mid": v(47.67, -8.79) * mm, "end": v(47.48, -8.9) * mm});
            skLineSegment(sketch, "E50.43.11", {"start": v(46.6, -9.1) * mm, "end": v(47.48, -8.9) * mm});
            skArc(sketch, "E50.43.12", {"start": v(46.3, -9.39) * mm, "mid": v(46.4, -9.2) * mm, "end": v(46.6, -9.1) * mm});
            skLineSegment(sketch, "E50.43.13", {"start": v(46.21, -9.82) * mm, "end": v(46.3, -9.39) * mm});
            skLineSegment(sketch, "E50.44.0", {"start": v(46.99, -4.94) * mm, "end": v(46.94, -5.38) * mm});
            skArc(sketch, "E50.44.1", {"start": v(46.94, -5.38) * mm, "mid": v(46.98, -5.59) * mm, "end": v(47.12, -5.75) * mm});
            skLineSegment(sketch, "E50.44.2", {"start": v(47.12, -5.75) * mm, "end": v(47.9, -6.22) * mm});
            skArc(sketch, "E50.44.3", {"start": v(48.09, -6.58) * mm, "mid": v(48.05, -6.37) * mm, "end": v(47.9, -6.22) * mm});
            skLineSegment(sketch, "E50.44.4", {"start": v(48.09, -6.58) * mm, "end": v(47.93, -8.1) * mm});
            skLineSegment(sketch, "E50.44.5", {"start": v(47.93, -8.1) * mm, "end": v(48.94, -8.2) * mm});
            skLineSegment(sketch, "E50.44.6", {"start": v(48.94, -8.2) * mm, "end": v(49.26, -5.18) * mm});
            skLineSegment(sketch, "E50.44.7", {"start": v(49.58, -2.15) * mm, "end": v(49.26, -5.18) * mm});
            skLineSegment(sketch, "E50.44.8", {"start": v(48.57, -2.04) * mm, "end": v(49.58, -2.15) * mm});
            skLineSegment(sketch, "E50.44.9", {"start": v(48.4, -3.56) * mm, "end": v(48.57, -2.04) * mm});
            skArc(sketch, "E50.44.10", {"start": v(48.4, -3.56) * mm, "mid": v(48.33, -3.76) * mm, "end": v(48.15, -3.88) * mm});
            skLineSegment(sketch, "E50.44.11", {"start": v(47.29, -4.18) * mm, "end": v(48.15, -3.88) * mm});
            skArc(sketch, "E50.44.12", {"start": v(47.03, -4.5) * mm, "mid": v(47.11, -4.3) * mm, "end": v(47.29, -4.18) * mm});
            skLineSegment(sketch, "E50.44.13", {"start": v(46.99, -4.94) * mm, "end": v(47.03, -4.5) * mm});
            skLineSegment(sketch, "E50.45.0", {"start": v(47.24, 0) * mm, "end": v(47.24, -0.44) * mm});
            skArc(sketch, "E50.45.1", {"start": v(47.24, -0.44) * mm, "mid": v(47.3, -0.65) * mm, "end": v(47.46, -0.79) * mm});
            skLineSegment(sketch, "E50.45.2", {"start": v(47.46, -0.79) * mm, "end": v(48.3, -1.18) * mm});
            skArc(sketch, "E50.45.3", {"start": v(48.51, -1.52) * mm, "mid": v(48.45, -1.32) * mm, "end": v(48.3, -1.18) * mm});
            skLineSegment(sketch, "E50.45.4", {"start": v(48.51, -1.52) * mm, "end": v(48.51, -3.05) * mm});
            skLineSegment(sketch, "E50.45.5", {"start": v(48.51, -3.05) * mm, "end": v(49.53, -3.05) * mm});
            skLineSegment(sketch, "E50.45.6", {"start": v(49.53, -3.05) * mm, "end": v(49.53, 0) * mm});
            skLineSegment(sketch, "E50.45.7", {"start": v(49.53, 3.05) * mm, "end": v(49.53, 0) * mm});
            skLineSegment(sketch, "E50.45.8", {"start": v(48.51, 3.05) * mm, "end": v(49.53, 3.05) * mm});
            skLineSegment(sketch, "E50.45.9", {"start": v(48.51, 1.52) * mm, "end": v(48.51, 3.05) * mm});
            skArc(sketch, "E50.45.10", {"start": v(48.51, 1.52) * mm, "mid": v(48.45, 1.32) * mm, "end": v(48.3, 1.18) * mm});
            skLineSegment(sketch, "E50.45.11", {"start": v(47.46, 0.79) * mm, "end": v(48.3, 1.18) * mm});
            skArc(sketch, "E50.45.12", {"start": v(47.24, 0.44) * mm, "mid": v(47.3, 0.65) * mm, "end": v(47.46, 0.79) * mm});
            skLineSegment(sketch, "E50.45.13", {"start": v(47.24, 0) * mm, "end": v(47.24, 0.44) * mm});
            skLineSegment(sketch, "E50.46.0", {"start": v(46.99, 4.94) * mm, "end": v(47.03, 4.5) * mm});
            skArc(sketch, "E50.46.1", {"start": v(47.03, 4.5) * mm, "mid": v(47.11, 4.3) * mm, "end": v(47.29, 4.18) * mm});
            skLineSegment(sketch, "E50.46.2", {"start": v(47.29, 4.18) * mm, "end": v(48.15, 3.88) * mm});
            skArc(sketch, "E50.46.3", {"start": v(48.4, 3.56) * mm, "mid": v(48.33, 3.76) * mm, "end": v(48.15, 3.88) * mm});
            skLineSegment(sketch, "E50.46.4", {"start": v(48.4, 3.56) * mm, "end": v(48.57, 2.04) * mm});
            skLineSegment(sketch, "E50.46.5", {"start": v(48.57, 2.04) * mm, "end": v(49.58, 2.15) * mm});
            skLineSegment(sketch, "E50.46.6", {"start": v(49.58, 2.15) * mm, "end": v(49.26, 5.18) * mm});
            skLineSegment(sketch, "E50.46.7", {"start": v(48.94, 8.2) * mm, "end": v(49.26, 5.18) * mm});
            skLineSegment(sketch, "E50.46.8", {"start": v(47.93, 8.1) * mm, "end": v(48.94, 8.2) * mm});
            skLineSegment(sketch, "E50.46.9", {"start": v(48.09, 6.58) * mm, "end": v(47.93, 8.1) * mm});
            skArc(sketch, "E50.46.10", {"start": v(48.09, 6.58) * mm, "mid": v(48.05, 6.37) * mm, "end": v(47.9, 6.22) * mm});
            skLineSegment(sketch, "E50.46.11", {"start": v(47.12, 5.75) * mm, "end": v(47.9, 6.22) * mm});
            skArc(sketch, "E50.46.12", {"start": v(46.94, 5.38) * mm, "mid": v(46.98, 5.59) * mm, "end": v(47.12, 5.75) * mm});
            skLineSegment(sketch, "E50.46.13", {"start": v(46.99, 4.94) * mm, "end": v(46.94, 5.38) * mm});
            skLineSegment(sketch, "E50.47.0", {"start": v(46.21, 9.82) * mm, "end": v(46.3, 9.39) * mm});
            skArc(sketch, "E50.47.1", {"start": v(46.3, 9.39) * mm, "mid": v(46.4, 9.2) * mm, "end": v(46.6, 9.1) * mm});
            skLineSegment(sketch, "E50.47.2", {"start": v(46.6, 9.1) * mm, "end": v(47.48, 8.9) * mm});
            skArc(sketch, "E50.47.3", {"start": v(47.77, 8.6) * mm, "mid": v(47.67, 8.79) * mm, "end": v(47.48, 8.9) * mm});
            skLineSegment(sketch, "E50.47.4", {"start": v(47.77, 8.6) * mm, "end": v(48.09, 7.1) * mm});
            skLineSegment(sketch, "E50.47.5", {"start": v(48.09, 7.1) * mm, "end": v(49.08, 7.32) * mm});
            skLineSegment(sketch, "E50.47.6", {"start": v(49.08, 7.32) * mm, "end": v(48.45, 10.3) * mm});
            skLineSegment(sketch, "E50.47.7", {"start": v(47.81, 13.28) * mm, "end": v(48.45, 10.3) * mm});
            skLineSegment(sketch, "E50.47.8", {"start": v(46.82, 13.07) * mm, "end": v(47.81, 13.28) * mm});
            skLineSegment(sketch, "E50.47.9", {"start": v(47.14, 11.57) * mm, "end": v(46.82, 13.07) * mm});
            skArc(sketch, "E50.47.10", {"start": v(47.14, 11.57) * mm, "mid": v(47.12, 11.36) * mm, "end": v(47, 11.2) * mm});
            skLineSegment(sketch, "E50.47.11", {"start": v(46.26, 10.64) * mm, "end": v(47, 11.2) * mm});
            skArc(sketch, "E50.47.12", {"start": v(46.12, 10.26) * mm, "mid": v(46.14, 10.47) * mm, "end": v(46.26, 10.64) * mm});
            skLineSegment(sketch, "E50.47.13", {"start": v(46.21, 9.82) * mm, "end": v(46.12, 10.26) * mm});
            skLineSegment(sketch, "E50.48.0", {"start": v(44.93, 14.6) * mm, "end": v(45.07, 14.18) * mm});
            skArc(sketch, "E50.48.1", {"start": v(45.07, 14.18) * mm, "mid": v(45.19, 14) * mm, "end": v(45.38, 13.92) * mm});
            skLineSegment(sketch, "E50.48.2", {"start": v(45.38, 13.92) * mm, "end": v(46.3, 13.8) * mm});
            skArc(sketch, "E50.48.3", {"start": v(46.6, 13.55) * mm, "mid": v(46.49, 13.72) * mm, "end": v(46.3, 13.8) * mm});
            skLineSegment(sketch, "E50.48.4", {"start": v(46.6, 13.55) * mm, "end": v(47.08, 12.1) * mm});
            skLineSegment(sketch, "E50.48.5", {"start": v(47.08, 12.1) * mm, "end": v(48.05, 12.4) * mm});
            skLineSegment(sketch, "E50.48.6", {"start": v(48.05, 12.4) * mm, "end": v(47.1, 15.3) * mm});
            skLineSegment(sketch, "E50.48.7", {"start": v(46.16, 18.2) * mm, "end": v(47.1, 15.3) * mm});
            skLineSegment(sketch, "E50.48.8", {"start": v(45.2, 17.9) * mm, "end": v(46.16, 18.2) * mm});
            skLineSegment(sketch, "E50.48.9", {"start": v(45.67, 16.44) * mm, "end": v(45.2, 17.9) * mm});
            skArc(sketch, "E50.48.10", {"start": v(45.67, 16.44) * mm, "mid": v(45.68, 16.22) * mm, "end": v(45.57, 16.04) * mm});
            skLineSegment(sketch, "E50.48.11", {"start": v(44.9, 15.42) * mm, "end": v(45.57, 16.04) * mm});
            skArc(sketch, "E50.48.12", {"start": v(44.8, 15.02) * mm, "mid": v(44.79, 15.23) * mm, "end": v(44.9, 15.42) * mm});
            skLineSegment(sketch, "E50.48.13", {"start": v(44.93, 14.6) * mm, "end": v(44.8, 15.02) * mm});
            skLineSegment(sketch, "E50.49.0", {"start": v(43.16, 19.22) * mm, "end": v(43.34, 18.81) * mm});
            skArc(sketch, "E50.49.1", {"start": v(43.34, 18.81) * mm, "mid": v(43.48, 18.65) * mm, "end": v(43.68, 18.59) * mm});
            skLineSegment(sketch, "E50.49.2", {"start": v(43.68, 18.59) * mm, "end": v(44.6, 18.57) * mm});
            skArc(sketch, "E50.49.3", {"start": v(44.94, 18.34) * mm, "mid": v(44.8, 18.5) * mm, "end": v(44.6, 18.57) * mm});
            skLineSegment(sketch, "E50.49.4", {"start": v(44.94, 18.34) * mm, "end": v(45.56, 16.95) * mm});
            skLineSegment(sketch, "E50.49.5", {"start": v(45.56, 16.95) * mm, "end": v(46.49, 17.36) * mm});
            skLineSegment(sketch, "E50.49.6", {"start": v(46.49, 17.36) * mm, "end": v(45.25, 20.15) * mm});
            skLineSegment(sketch, "E50.49.7", {"start": v(44, 22.93) * mm, "end": v(45.25, 20.15) * mm});
            skLineSegment(sketch, "E50.49.8", {"start": v(43.08, 22.52) * mm, "end": v(44, 22.93) * mm});
            skLineSegment(sketch, "E50.49.9", {"start": v(43.7, 21.12) * mm, "end": v(43.08, 22.52) * mm});
            skArc(sketch, "E50.49.10", {"start": v(43.7, 21.12) * mm, "mid": v(43.73, 20.91) * mm, "end": v(43.64, 20.72) * mm});
            skLineSegment(sketch, "E50.49.11", {"start": v(43.04, 20.03) * mm, "end": v(43.64, 20.72) * mm});
            skArc(sketch, "E50.49.12", {"start": v(42.98, 19.62) * mm, "mid": v(42.95, 19.83) * mm, "end": v(43.04, 20.03) * mm});
            skLineSegment(sketch, "E50.49.13", {"start": v(43.16, 19.22) * mm, "end": v(42.98, 19.62) * mm});
            skLineSegment(sketch, "E50.50.0", {"start": v(40.91, 23.62) * mm, "end": v(41.14, 23.24) * mm});
            skArc(sketch, "E50.50.1", {"start": v(41.14, 23.24) * mm, "mid": v(41.3, 23.1) * mm, "end": v(41.5, 23.05) * mm});
            skLineSegment(sketch, "E50.50.2", {"start": v(41.5, 23.05) * mm, "end": v(42.41, 23.13) * mm});
            skArc(sketch, "E50.50.3", {"start": v(42.77, 22.94) * mm, "mid": v(42.62, 23.09) * mm, "end": v(42.41, 23.13) * mm});
            skLineSegment(sketch, "E50.50.4", {"start": v(42.77, 22.94) * mm, "end": v(43.54, 21.62) * mm});
            skLineSegment(sketch, "E50.50.5", {"start": v(43.54, 21.62) * mm, "end": v(44.42, 22.13) * mm});
            skLineSegment(sketch, "E50.50.6", {"start": v(44.42, 22.13) * mm, "end": v(42.9, 24.77) * mm});
            skLineSegment(sketch, "E50.50.7", {"start": v(41.37, 27.4) * mm, "end": v(42.9, 24.77) * mm});
            skLineSegment(sketch, "E50.50.8", {"start": v(40.5, 26.9) * mm, "end": v(41.37, 27.4) * mm});
            skLineSegment(sketch, "E50.50.9", {"start": v(41.25, 25.57) * mm, "end": v(40.5, 26.9) * mm});
            skArc(sketch, "E50.50.10", {"start": v(41.25, 25.57) * mm, "mid": v(41.3, 25.37) * mm, "end": v(41.24, 25.16) * mm});
            skLineSegment(sketch, "E50.50.11", {"start": v(40.71, 24.41) * mm, "end": v(41.24, 25.16) * mm});
            skArc(sketch, "E50.50.12", {"start": v(40.7, 24) * mm, "mid": v(40.64, 24.21) * mm, "end": v(40.71, 24.41) * mm});
            skLineSegment(sketch, "E50.50.13", {"start": v(40.91, 23.62) * mm, "end": v(40.7, 24) * mm});
            skLineSegment(sketch, "E50.51.0", {"start": v(38.22, 27.77) * mm, "end": v(38.48, 27.41) * mm});
            skArc(sketch, "E50.51.1", {"start": v(38.48, 27.41) * mm, "mid": v(38.65, 27.28) * mm, "end": v(38.86, 27.26) * mm});
            skLineSegment(sketch, "E50.51.2", {"start": v(38.86, 27.26) * mm, "end": v(39.76, 27.44) * mm});
            skArc(sketch, "E50.51.3", {"start": v(40.14, 27.29) * mm, "mid": v(39.97, 27.42) * mm, "end": v(39.76, 27.44) * mm});
            skLineSegment(sketch, "E50.51.4", {"start": v(40.14, 27.29) * mm, "end": v(41.04, 26.05) * mm});
            skLineSegment(sketch, "E50.51.5", {"start": v(41.04, 26.05) * mm, "end": v(41.86, 26.65) * mm});
            skLineSegment(sketch, "E50.51.6", {"start": v(41.86, 26.65) * mm, "end": v(40.07, 29.11) * mm});
            skLineSegment(sketch, "E50.51.7", {"start": v(38.28, 31.58) * mm, "end": v(40.07, 29.11) * mm});
            skLineSegment(sketch, "E50.51.8", {"start": v(37.46, 30.98) * mm, "end": v(38.28, 31.58) * mm});
            skLineSegment(sketch, "E50.51.9", {"start": v(38.35, 29.75) * mm, "end": v(37.46, 30.98) * mm});
            skArc(sketch, "E50.51.10", {"start": v(38.35, 29.75) * mm, "mid": v(38.43, 29.55) * mm, "end": v(38.38, 29.34) * mm});
            skLineSegment(sketch, "E50.51.11", {"start": v(37.94, 28.54) * mm, "end": v(38.38, 29.34) * mm});
            skArc(sketch, "E50.51.12", {"start": v(37.96, 28.13) * mm, "mid": v(37.89, 28.33) * mm, "end": v(37.94, 28.54) * mm});
            skLineSegment(sketch, "E50.51.13", {"start": v(38.22, 27.77) * mm, "end": v(37.96, 28.13) * mm});
            skLineSegment(sketch, "E50.52.0", {"start": v(35.1, 31.61) * mm, "end": v(35.4, 31.28) * mm});
            skArc(sketch, "E50.52.1", {"start": v(35.4, 31.28) * mm, "mid": v(35.59, 31.17) * mm, "end": v(35.8, 31.17) * mm});
            skLineSegment(sketch, "E50.52.2", {"start": v(35.8, 31.17) * mm, "end": v(36.68, 31.44) * mm});
            skArc(sketch, "E50.52.3", {"start": v(37.07, 31.33) * mm, "mid": v(36.89, 31.44) * mm, "end": v(36.68, 31.44) * mm});
            skLineSegment(sketch, "E50.52.4", {"start": v(37.07, 31.33) * mm, "end": v(38.1, 30.2) * mm});
            skLineSegment(sketch, "E50.52.5", {"start": v(38.1, 30.2) * mm, "end": v(38.85, 30.88) * mm});
            skLineSegment(sketch, "E50.52.6", {"start": v(38.85, 30.88) * mm, "end": v(36.8, 33.14) * mm});
            skLineSegment(sketch, "E50.52.7", {"start": v(34.77, 35.4) * mm, "end": v(36.8, 33.14) * mm});
            skLineSegment(sketch, "E50.52.8", {"start": v(34.01, 34.73) * mm, "end": v(34.77, 35.4) * mm});
            skLineSegment(sketch, "E50.52.9", {"start": v(35.04, 33.6) * mm, "end": v(34.01, 34.73) * mm});
            skArc(sketch, "E50.52.10", {"start": v(35.04, 33.6) * mm, "mid": v(35.13, 33.4) * mm, "end": v(35.1, 33.19) * mm});
            skLineSegment(sketch, "E50.52.11", {"start": v(34.75, 32.35) * mm, "end": v(35.1, 33.19) * mm});
            skArc(sketch, "E50.52.12", {"start": v(34.81, 31.94) * mm, "mid": v(34.72, 32.13) * mm, "end": v(34.75, 32.35) * mm});
            skLineSegment(sketch, "E50.52.13", {"start": v(35.1, 31.61) * mm, "end": v(34.81, 31.94) * mm});
            skLineSegment(sketch, "E50.53.0", {"start": v(31.61, 35.1) * mm, "end": v(31.94, 34.81) * mm});
            skArc(sketch, "E50.53.1", {"start": v(31.94, 34.81) * mm, "mid": v(32.13, 34.72) * mm, "end": v(32.35, 34.75) * mm});
            skLineSegment(sketch, "E50.53.2", {"start": v(32.35, 34.75) * mm, "end": v(33.19, 35.1) * mm});
            skArc(sketch, "E50.53.3", {"start": v(33.6, 35.04) * mm, "mid": v(33.4, 35.13) * mm, "end": v(33.19, 35.1) * mm});
            skLineSegment(sketch, "E50.53.4", {"start": v(33.6, 35.04) * mm, "end": v(34.73, 34.01) * mm});
            skLineSegment(sketch, "E50.53.5", {"start": v(34.73, 34.01) * mm, "end": v(35.4, 34.77) * mm});
            skLineSegment(sketch, "E50.53.6", {"start": v(35.4, 34.77) * mm, "end": v(33.14, 36.8) * mm});
            skLineSegment(sketch, "E50.53.7", {"start": v(30.88, 38.85) * mm, "end": v(33.14, 36.8) * mm});
            skLineSegment(sketch, "E50.53.8", {"start": v(30.2, 38.1) * mm, "end": v(30.88, 38.85) * mm});
            skLineSegment(sketch, "E50.53.9", {"start": v(31.33, 37.07) * mm, "end": v(30.2, 38.1) * mm});
            skArc(sketch, "E50.53.10", {"start": v(31.33, 37.07) * mm, "mid": v(31.44, 36.89) * mm, "end": v(31.44, 36.68) * mm});
            skLineSegment(sketch, "E50.53.11", {"start": v(31.17, 35.8) * mm, "end": v(31.44, 36.68) * mm});
            skArc(sketch, "E50.53.12", {"start": v(31.28, 35.4) * mm, "mid": v(31.17, 35.59) * mm, "end": v(31.17, 35.8) * mm});
            skLineSegment(sketch, "E50.53.13", {"start": v(31.61, 35.1) * mm, "end": v(31.28, 35.4) * mm});
            skLineSegment(sketch, "E50.54.0", {"start": v(27.77, 38.22) * mm, "end": v(28.13, 37.96) * mm});
            skArc(sketch, "E50.54.1", {"start": v(28.13, 37.96) * mm, "mid": v(28.33, 37.89) * mm, "end": v(28.54, 37.94) * mm});
            skLineSegment(sketch, "E50.54.2", {"start": v(28.54, 37.94) * mm, "end": v(29.34, 38.38) * mm});
            skArc(sketch, "E50.54.3", {"start": v(29.75, 38.35) * mm, "mid": v(29.55, 38.43) * mm, "end": v(29.34, 38.38) * mm});
            skLineSegment(sketch, "E50.54.4", {"start": v(29.75, 38.35) * mm, "end": v(30.98, 37.46) * mm});
            skLineSegment(sketch, "E50.54.5", {"start": v(30.98, 37.46) * mm, "end": v(31.58, 38.28) * mm});
            skLineSegment(sketch, "E50.54.6", {"start": v(31.58, 38.28) * mm, "end": v(29.11, 40.07) * mm});
            skLineSegment(sketch, "E50.54.7", {"start": v(26.65, 41.86) * mm, "end": v(29.11, 40.07) * mm});
            skLineSegment(sketch, "E50.54.8", {"start": v(26.05, 41.04) * mm, "end": v(26.65, 41.86) * mm});
            skLineSegment(sketch, "E50.54.9", {"start": v(27.29, 40.14) * mm, "end": v(26.05, 41.04) * mm});
            skArc(sketch, "E50.54.10", {"start": v(27.29, 40.14) * mm, "mid": v(27.42, 39.97) * mm, "end": v(27.44, 39.76) * mm});
            skLineSegment(sketch, "E50.54.11", {"start": v(27.26, 38.86) * mm, "end": v(27.44, 39.76) * mm});
            skArc(sketch, "E50.54.12", {"start": v(27.41, 38.48) * mm, "mid": v(27.28, 38.65) * mm, "end": v(27.26, 38.86) * mm});
            skLineSegment(sketch, "E50.54.13", {"start": v(27.77, 38.22) * mm, "end": v(27.41, 38.48) * mm});
            skLineSegment(sketch, "E50.55.0", {"start": v(23.62, 40.91) * mm, "end": v(24, 40.7) * mm});
            skArc(sketch, "E50.55.1", {"start": v(24, 40.7) * mm, "mid": v(24.21, 40.64) * mm, "end": v(24.41, 40.71) * mm});
            skLineSegment(sketch, "E50.55.2", {"start": v(24.41, 40.71) * mm, "end": v(25.16, 41.24) * mm});
            skArc(sketch, "E50.55.3", {"start": v(25.57, 41.25) * mm, "mid": v(25.37, 41.3) * mm, "end": v(25.16, 41.24) * mm});
            skLineSegment(sketch, "E50.55.4", {"start": v(25.57, 41.25) * mm, "end": v(26.9, 40.5) * mm});
            skLineSegment(sketch, "E50.55.5", {"start": v(26.9, 40.5) * mm, "end": v(27.4, 41.37) * mm});
            skLineSegment(sketch, "E50.55.6", {"start": v(27.4, 41.37) * mm, "end": v(24.76, 42.9) * mm});
            skLineSegment(sketch, "E50.55.7", {"start": v(22.13, 44.42) * mm, "end": v(24.77, 42.9) * mm});
            skLineSegment(sketch, "E50.55.8", {"start": v(21.62, 43.54) * mm, "end": v(22.13, 44.42) * mm});
            skLineSegment(sketch, "E50.55.9", {"start": v(22.94, 42.77) * mm, "end": v(21.62, 43.54) * mm});
            skArc(sketch, "E50.55.10", {"start": v(22.94, 42.77) * mm, "mid": v(23.09, 42.62) * mm, "end": v(23.13, 42.41) * mm});
            skLineSegment(sketch, "E50.55.11", {"start": v(23.05, 41.5) * mm, "end": v(23.13, 42.41) * mm});
            skArc(sketch, "E50.55.12", {"start": v(23.24, 41.14) * mm, "mid": v(23.1, 41.3) * mm, "end": v(23.05, 41.5) * mm});
            skLineSegment(sketch, "E50.55.13", {"start": v(23.62, 40.91) * mm, "end": v(23.24, 41.14) * mm});
            skLineSegment(sketch, "E50.56.0", {"start": v(19.22, 43.16) * mm, "end": v(19.62, 42.98) * mm});
            skArc(sketch, "E50.56.1", {"start": v(19.62, 42.98) * mm, "mid": v(19.83, 42.95) * mm, "end": v(20.03, 43.04) * mm});
            skLineSegment(sketch, "E50.56.2", {"start": v(20.03, 43.04) * mm, "end": v(20.72, 43.64) * mm});
            skArc(sketch, "E50.56.3", {"start": v(21.12, 43.7) * mm, "mid": v(20.91, 43.73) * mm, "end": v(20.72, 43.64) * mm});
            skLineSegment(sketch, "E50.56.4", {"start": v(21.12, 43.7) * mm, "end": v(22.52, 43.08) * mm});
            skLineSegment(sketch, "E50.56.5", {"start": v(22.52, 43.08) * mm, "end": v(22.93, 44) * mm});
            skLineSegment(sketch, "E50.56.6", {"start": v(22.93, 44) * mm, "end": v(20.15, 45.25) * mm});
            skLineSegment(sketch, "E50.56.7", {"start": v(17.36, 46.49) * mm, "end": v(20.15, 45.25) * mm});
            skLineSegment(sketch, "E50.56.8", {"start": v(16.95, 45.56) * mm, "end": v(17.36, 46.49) * mm});
            skLineSegment(sketch, "E50.56.9", {"start": v(18.34, 44.94) * mm, "end": v(16.95, 45.56) * mm});
            skArc(sketch, "E50.56.10", {"start": v(18.34, 44.94) * mm, "mid": v(18.5, 44.8) * mm, "end": v(18.57, 44.6) * mm});
            skLineSegment(sketch, "E50.56.11", {"start": v(18.59, 43.68) * mm, "end": v(18.57, 44.6) * mm});
            skArc(sketch, "E50.56.12", {"start": v(18.81, 43.34) * mm, "mid": v(18.65, 43.48) * mm, "end": v(18.59, 43.68) * mm});
            skLineSegment(sketch, "E50.56.13", {"start": v(19.22, 43.16) * mm, "end": v(18.81, 43.34) * mm});
            skLineSegment(sketch, "E50.57.0", {"start": v(14.6, 44.93) * mm, "end": v(15.02, 44.8) * mm});
            skArc(sketch, "E50.57.1", {"start": v(15.02, 44.8) * mm, "mid": v(15.23, 44.79) * mm, "end": v(15.42, 44.9) * mm});
            skLineSegment(sketch, "E50.57.2", {"start": v(15.42, 44.9) * mm, "end": v(16.04, 45.57) * mm});
            skArc(sketch, "E50.57.3", {"start": v(16.44, 45.67) * mm, "mid": v(16.22, 45.68) * mm, "end": v(16.04, 45.57) * mm});
            skLineSegment(sketch, "E50.57.4", {"start": v(16.44, 45.67) * mm, "end": v(17.9, 45.2) * mm});
            skLineSegment(sketch, "E50.57.5", {"start": v(17.9, 45.2) * mm, "end": v(18.2, 46.16) * mm});
            skLineSegment(sketch, "E50.57.6", {"start": v(18.2, 46.16) * mm, "end": v(15.3, 47.1) * mm});
            skLineSegment(sketch, "E50.57.7", {"start": v(12.4, 48.05) * mm, "end": v(15.3, 47.1) * mm});
            skLineSegment(sketch, "E50.57.8", {"start": v(12.1, 47.08) * mm, "end": v(12.4, 48.05) * mm});
            skLineSegment(sketch, "E50.57.9", {"start": v(13.55, 46.6) * mm, "end": v(12.1, 47.08) * mm});
            skArc(sketch, "E50.57.10", {"start": v(13.55, 46.6) * mm, "mid": v(13.72, 46.49) * mm, "end": v(13.8, 46.3) * mm});
            skLineSegment(sketch, "E50.57.11", {"start": v(13.92, 45.38) * mm, "end": v(13.8, 46.3) * mm});
            skArc(sketch, "E50.57.12", {"start": v(14.18, 45.07) * mm, "mid": v(14, 45.19) * mm, "end": v(13.92, 45.38) * mm});
            skLineSegment(sketch, "E50.57.13", {"start": v(14.6, 44.93) * mm, "end": v(14.18, 45.07) * mm});
            skLineSegment(sketch, "E50.58.0", {"start": v(9.82, 46.21) * mm, "end": v(10.26, 46.12) * mm});
            skArc(sketch, "E50.58.1", {"start": v(10.26, 46.12) * mm, "mid": v(10.47, 46.14) * mm, "end": v(10.64, 46.26) * mm});
            skLineSegment(sketch, "E50.58.2", {"start": v(10.64, 46.26) * mm, "end": v(11.2, 47) * mm});
            skArc(sketch, "E50.58.3", {"start": v(11.57, 47.14) * mm, "mid": v(11.36, 47.12) * mm, "end": v(11.2, 47) * mm});
            skLineSegment(sketch, "E50.58.4", {"start": v(11.57, 47.14) * mm, "end": v(13.07, 46.82) * mm});
            skLineSegment(sketch, "E50.58.5", {"start": v(13.07, 46.82) * mm, "end": v(13.28, 47.81) * mm});
            skLineSegment(sketch, "E50.58.6", {"start": v(13.28, 47.81) * mm, "end": v(10.3, 48.45) * mm});
            skLineSegment(sketch, "E50.58.7", {"start": v(7.32, 49.08) * mm, "end": v(10.3, 48.45) * mm});
            skLineSegment(sketch, "E50.58.8", {"start": v(7.1, 48.09) * mm, "end": v(7.32, 49.08) * mm});
            skLineSegment(sketch, "E50.58.9", {"start": v(8.6, 47.77) * mm, "end": v(7.1, 48.09) * mm});
            skArc(sketch, "E50.58.10", {"start": v(8.6, 47.77) * mm, "mid": v(8.79, 47.67) * mm, "end": v(8.9, 47.48) * mm});
            skLineSegment(sketch, "E50.58.11", {"start": v(9.1, 46.6) * mm, "end": v(8.9, 47.48) * mm});
            skArc(sketch, "E50.58.12", {"start": v(9.39, 46.3) * mm, "mid": v(9.2, 46.4) * mm, "end": v(9.1, 46.6) * mm});
            skLineSegment(sketch, "E50.58.13", {"start": v(9.82, 46.21) * mm, "end": v(9.39, 46.3) * mm});
            skLineSegment(sketch, "E50.59.0", {"start": v(4.94, 46.99) * mm, "end": v(5.38, 46.94) * mm});
            skArc(sketch, "E50.59.1", {"start": v(5.38, 46.94) * mm, "mid": v(5.59, 46.98) * mm, "end": v(5.75, 47.12) * mm});
            skLineSegment(sketch, "E50.59.2", {"start": v(5.75, 47.12) * mm, "end": v(6.22, 47.9) * mm});
            skArc(sketch, "E50.59.3", {"start": v(6.58, 48.09) * mm, "mid": v(6.37, 48.05) * mm, "end": v(6.22, 47.9) * mm});
            skLineSegment(sketch, "E50.59.4", {"start": v(6.58, 48.09) * mm, "end": v(8.1, 47.93) * mm});
            skLineSegment(sketch, "E50.59.5", {"start": v(8.1, 47.93) * mm, "end": v(8.2, 48.94) * mm});
            skLineSegment(sketch, "E50.59.6", {"start": v(8.2, 48.94) * mm, "end": v(5.18, 49.26) * mm});
            skLineSegment(sketch, "E50.59.7", {"start": v(2.15, 49.58) * mm, "end": v(5.18, 49.26) * mm});
            skLineSegment(sketch, "E50.59.8", {"start": v(2.04, 48.57) * mm, "end": v(2.15, 49.58) * mm});
            skLineSegment(sketch, "E50.59.9", {"start": v(3.56, 48.4) * mm, "end": v(2.04, 48.57) * mm});
            skArc(sketch, "E50.59.10", {"start": v(3.56, 48.4) * mm, "mid": v(3.76, 48.33) * mm, "end": v(3.88, 48.15) * mm});
            skLineSegment(sketch, "E50.59.11", {"start": v(4.18, 47.29) * mm, "end": v(3.88, 48.15) * mm});
            skArc(sketch, "E50.59.12", {"start": v(4.5, 47.03) * mm, "mid": v(4.3, 47.11) * mm, "end": v(4.18, 47.29) * mm});
            skLineSegment(sketch, "E50.59.13", {"start": v(4.94, 46.99) * mm, "end": v(4.5, 47.03) * mm});
            skCircle(sketch, "E51.0", {"center": v(0, 0) * mm, "radius": 50.3 * mm});
            skSolve(sketch);
        }
        {
            var Q0;
            Q0=makeQuery(id+"F8.imprint","IMPRINT",FACE,{"disambiguationData":[TD([[makeQuery(id+"F8.imprint","IMPRINT",EDGE,{"derivedFrom":sQuery(id+"F8.wireOp",EDGE,"E23.0.0")}),-1.0]])]});
            var Q1;
            Q1=makeQuery(id+"F8.imprint","IMPRINT",FACE,{"disambiguationData":[TD([[makeQuery(id+"F8.imprint","IMPRINT",EDGE,{"derivedFrom":sQuery(id+"F8.wireOp",EDGE,"E23.0.0")}),1.0]])]});
            extrude(context, id + "F9", {"entities" : qUnion([Q0, Q1]), "depth" : 3.17 * mm});
        }
        {
            var Q0;
            Q0=qCreatedBy(makeId("Top.planeOp"),FACE);
            var sketch = newSketch(context, id + "F10", { "sketchPlane" : qUnion([Q0])});
            skCircle(sketch, "E52.0", {"center": v(0, 0) * mm, "radius": 38.1 * mm});
            skArc(sketch, "E53.0.0", {"start": v(-7.57, 42.92) * mm, "mid": v(-30.82, 30.82) * mm, "end": v(-42.92, 7.57) * mm});
            skArc(sketch, "E53.0.1", {"start": v(-42.92, 7.57) * mm, "mid": v(-41.38, 5.36) * mm, "end": v(-39.17, 6.9) * mm});
            skArc(sketch, "E53.0.2", {"start": v(-39.17, 6.9) * mm, "mid": v(-28.12, 28.12) * mm, "end": v(-6.9, 39.17) * mm});
            skArc(sketch, "E53.0.3", {"start": v(-6.9, 39.17) * mm, "mid": v(-5.36, 41.38) * mm, "end": v(-7.57, 42.92) * mm});
            skCircle(sketch, "E54.0", {"center": v(-41.68, 0) * mm, "radius": 1.9 * mm});
            skArc(sketch, "E55.0.0", {"start": v(-42.92, -7.57) * mm, "mid": v(-30.82, -30.82) * mm, "end": v(-7.57, -42.92) * mm});
            skArc(sketch, "E55.0.1", {"start": v(-7.57, -42.92) * mm, "mid": v(-5.36, -41.38) * mm, "end": v(-6.9, -39.17) * mm});
            skArc(sketch, "E55.0.2", {"start": v(-6.9, -39.17) * mm, "mid": v(-28.12, -28.12) * mm, "end": v(-39.17, -6.9) * mm});
            skArc(sketch, "E55.0.3", {"start": v(-39.17, -6.9) * mm, "mid": v(-41.38, -5.36) * mm, "end": v(-42.92, -7.57) * mm});
            skCircle(sketch, "E56.0", {"center": v(0, -41.68) * mm, "radius": 1.9 * mm});
            skArc(sketch, "E57.0", {"start": v(7.57, -42.92) * mm, "mid": v(30.82, -30.82) * mm, "end": v(42.92, -7.57) * mm});
            skArc(sketch, "E58.0.1", {"start": v(42.92, -7.57) * mm, "mid": v(41.38, -5.36) * mm, "end": v(39.17, -6.9) * mm});
            skArc(sketch, "E58.0.2", {"start": v(39.17, -6.9) * mm, "mid": v(28.12, -28.12) * mm, "end": v(6.9, -39.17) * mm});
            skArc(sketch, "E58.0.3", {"start": v(6.9, -39.17) * mm, "mid": v(5.36, -41.38) * mm, "end": v(7.57, -42.92) * mm});
            skArc(sketch, "E59.0.0", {"start": v(39.17, 6.9) * mm, "mid": v(41.38, 5.36) * mm, "end": v(42.92, 7.57) * mm});
            skArc(sketch, "E59.0.1", {"start": v(42.92, 7.57) * mm, "mid": v(30.82, 30.82) * mm, "end": v(7.57, 42.92) * mm});
            skArc(sketch, "E59.0.2", {"start": v(7.57, 42.92) * mm, "mid": v(5.36, 41.38) * mm, "end": v(6.9, 39.17) * mm});
            skArc(sketch, "E59.0.3", {"start": v(6.9, 39.17) * mm, "mid": v(28.12, 28.12) * mm, "end": v(39.17, 6.9) * mm});
            skCircle(sketch, "E60.0", {"center": v(41.68, 0) * mm, "radius": 1.9 * mm});
            skCircle(sketch, "E61.0", {"center": v(0, 41.68) * mm, "radius": 1.9 * mm});
            skCircle(sketch, "E62.0", {"center": v(0, 0) * mm, "radius": 50.3 * mm});
            skSolve(sketch);
        }
        {
            var Q0;
            Q0=makeQuery(id+"F10.imprint","IMPRINT",FACE,{"disambiguationData":[TD([[makeQuery(id+"F10.imprint","IMPRINT",EDGE,{"derivedFrom":sQuery(id+"F10.wireOp",EDGE,"E52.0")}),-1.0]])]});
            extrude(context, id + "F11", {"entities" : qUnion([Q0]), "depth" : 2.54 * mm});
        }
        {
            var Q0;
            Q0=qCreatedBy(makeId("Front.planeOp"),FACE);
            var sketch = newSketch(context, id + "F12", { "sketchPlane" : qUnion([Q0])});
            skLineSegment(sketch, "E63", {"start": v(50.3, 1.11) * mm, "end": v(50.3, 0) * mm});
            skLineSegment(sketch, "E64.0", {"start": v(-50.3, 2.54) * mm, "end": v(47.45, 2.54) * mm});
            skPoint(sketch, "E65", {"position": v(47.75, 2.54) * mm});
            skPoint(sketch, "E66", {"position": v(50.3, 1.27) * mm});
            skLineSegment(sketch, "E67", {"start": v(48.02, 2.4) * mm, "end": v(50.15, 1.34) * mm});
            skPoint(sketch, "E68.orphan", {"position": v(50.3, 2.54) * mm});
            skArc(sketch, "E69.filletArc", {"start": v(48.02, 2.4) * mm, "mid": v(47.74, 2.5) * mm, "end": v(47.45, 2.54) * mm});
            skArc(sketch, "E70.filletArc", {"start": v(50.3, 1.11) * mm, "mid": v(50.25, 1.25) * mm, "end": v(50.15, 1.34) * mm});
            skLineSegment(sketch, "E71", {"start": v(50.3, 1.11) * mm, "end": v(51.11, 1.11) * mm});
            skLineSegment(sketch, "E72", {"start": v(51.11, 1.11) * mm, "end": v(51.11, 2.82) * mm});
            skLineSegment(sketch, "E73", {"start": v(51.11, 2.82) * mm, "end": v(47.45, 2.82) * mm});
            skLineSegment(sketch, "E74", {"start": v(47.45, 2.82) * mm, "end": v(47.45, 2.54) * mm});
            skSolve(sketch);
        }
        {
            var Q0;
            Q0=makeQuery(id+"F12.imprint","IMPRINT",FACE,{"disambiguationData":[TD([[makeQuery(id+"F12.imprint","IMPRINT",EDGE,{"derivedFrom":sQuery(id+"F12.wireOp",EDGE,"E67")}),1.0]])]});
            var Q1;
            Q1=makeQuery(id+"F11.opExtrude","CAP_EDGE",EDGE,{"disambiguationData":[OSD([sQuery(id+"F10.wireOp",EDGE,"E52.0")])],"isStart":true});
            revolve(context, id + "F13", {"operationType" : NewBodyOperationType.REMOVE, "entities" : qUnion([Q0]), "axis" : qUnion([Q1]), "revolveType" : RevolveType.FULL, "oppositeDirection" : true});
        }
        {
            var Q0;
            Q0=makeQuery(id+"F2.imprint","IMPRINT",FACE,{"disambiguationData":[TD([[makeQuery(id+"F2.imprint","IMPRINT",EDGE,{"derivedFrom":sQuery(id+"F2.wireOp",EDGE,"E22")}),1.0]])]});
            extrude(context, id + "F14", {"entities" : qUnion([Q0]), "depth" : 92.7 * mm});
        }
        {
            var Q0;
            Q0 = qSketchRegion(id + "F2", true);
            extrude(context, id + "F15", {"entities" : qUnion([Q0]), "depth" : 76.2 * mm});
        }
        {
            var Q0;
            Q0=qCreatedBy(makeId("Top.planeOp"),FACE);
            var sketch = newSketch(context, id + "F16", { "sketchPlane" : qUnion([Q0])});
            skLineSegment(sketch, "E75", {"start": v(0, 0) * mm, "end": v(51.64, -51.64) * mm, "construction": true});
            skCircle(sketch, "E76", {"center": v(51.64, -51.64) * mm, "radius": 18.41 * mm});
            skCircle(sketch, "E77", {"center": v(51.64, -51.64) * mm, "radius": 15.5 * mm, "construction": true});
            skLineSegment(sketch, "E78", {"start": v(51.64, -51.64) * mm, "end": v(62.6, -40.68) * mm, "construction": true});
            skCircle(sketch, "E79", {"center": v(62.6, -40.68) * mm, "radius": 1.5 * mm});
            skLineSegment(sketch, "E80", {"start": v(51.64, -51.64) * mm, "end": v(62.6, -62.6) * mm, "construction": true});
            skCircle(sketch, "E81", {"center": v(57.11, -57.11) * mm, "radius": 5.97 * mm});
            skCircle(sketch, "E82", {"center": v(57.11, -57.11) * mm, "radius": 3 * mm});
            skCircle(sketch, "E83.1.0", {"center": v(47.63, -36.67) * mm, "radius": 1.5 * mm});
            skCircle(sketch, "E83.2.0", {"center": v(36.67, -47.63) * mm, "radius": 1.5 * mm});
            skCircle(sketch, "E83.3.0", {"center": v(40.68, -62.6) * mm, "radius": 1.5 * mm});
            skCircle(sketch, "E83.4.0", {"center": v(55.65, -66.6) * mm, "radius": 1.5 * mm});
            skCircle(sketch, "E83.5.0", {"center": v(66.6, -55.65) * mm, "radius": 1.5 * mm});
            skCircle(sketch, "E84", {"center": v(51.64, -51.64) * mm, "radius": 16.51 * mm});
            skSolve(sketch);
        }
        {
            var Q0;
            Q0=makeQuery(id+"F16.imprint","IMPRINT",FACE,{"disambiguationData":[TD([[makeQuery(id+"F16.imprint","IMPRINT",EDGE,{"derivedFrom":sQuery(id+"F16.wireOp",EDGE,"E76")}),1.0]])]});
            var Q1;
            Q1=makeQuery(id+"F16.imprint","IMPRINT",FACE,{"disambiguationData":[TD([[makeQuery(id+"F16.imprint","IMPRINT",EDGE,{"derivedFrom":sQuery(id+"F16.wireOp",EDGE,"E81")}),-1.0]])]});
            extrude(context, id + "F17", {"entities" : qUnion([Q0, Q1]), "depth" : 17.78 * mm});
        }
        {
            var Q0;
            Q0=makeQuery(id+"F16.imprint","IMPRINT",FACE,{"disambiguationData":[TD([[makeQuery(id+"F16.imprint","IMPRINT",EDGE,{"derivedFrom":sQuery(id+"F16.wireOp",EDGE,"E81")}),1.0]])]});
            extrude(context, id + "F18", {"entities" : qUnion([Q0]), "operationType" : NewBodyOperationType.ADD, "depth" : 22.1 * mm});
        }
        {
            var Q0;
            Q0=makeQuery(id+"F16.imprint","IMPRINT",FACE,{"disambiguationData":[TD([[makeQuery(id+"F16.imprint","IMPRINT",EDGE,{"derivedFrom":sQuery(id+"F16.wireOp",EDGE,"E82")}),1.0]])]});
            extrude(context, id + "F19", {"entities" : qUnion([Q0]), "operationType" : NewBodyOperationType.ADD, "depth" : 40.26 * mm});
        }
        {
            var Q0;
            Q0=makeQuery(id+"F16.imprint","IMPRINT",FACE,{"disambiguationData":[TD([[makeQuery(id+"F16.imprint","IMPRINT",EDGE,{"derivedFrom":sQuery(id+"F16.wireOp",EDGE,"E81")}),-1.0]])]});
            var Q1;
            {var subQ0=sQuery(id+"F16.wireOp",EDGE,"E84");var subQ1=sQuery(id+"F16.wireOp",EDGE,"E83.3.0");var subQ2=makeQuery(id+"F16.imprint","INTERSECT",VERTEX,{"disambiguationData":[OD(0.0)],"derivedFrom":[subQ1,subQ0]});Q1=makeQuery(id+"F16.imprint","IMPRINT",FACE,{"disambiguationData":[TD([[makeQuery(id+"F16.imprint","IMPRINT",EDGE,{"disambiguationData":[TD([[subQ2,1.0]])],"derivedFrom":subQ1}),1.0]])]});}
            var Q2;
            {var subQ0=sQuery(id+"F16.wireOp",EDGE,"E84");var subQ1=sQuery(id+"F16.wireOp",EDGE,"E83.2.0");var subQ2=makeQuery(id+"F16.imprint","INTERSECT",VERTEX,{"disambiguationData":[OD(0.0)],"derivedFrom":[subQ1,subQ0]});Q2=makeQuery(id+"F16.imprint","IMPRINT",FACE,{"disambiguationData":[TD([[makeQuery(id+"F16.imprint","IMPRINT",EDGE,{"disambiguationData":[TD([[subQ2,1.0]])],"derivedFrom":subQ1}),1.0]])]});}
            var Q3;
            {var subQ0=sQuery(id+"F16.wireOp",EDGE,"E84");var subQ1=sQuery(id+"F16.wireOp",EDGE,"E83.4.0");var subQ2=makeQuery(id+"F16.imprint","INTERSECT",VERTEX,{"disambiguationData":[OD(0.0)],"derivedFrom":[subQ1,subQ0]});Q3=makeQuery(id+"F16.imprint","IMPRINT",FACE,{"disambiguationData":[TD([[makeQuery(id+"F16.imprint","IMPRINT",EDGE,{"disambiguationData":[TD([[subQ2,1.0]])],"derivedFrom":subQ1}),1.0]])]});}
            var Q4;
            {var subQ0=sQuery(id+"F16.wireOp",EDGE,"E84");var subQ1=sQuery(id+"F16.wireOp",EDGE,"E83.1.0");var subQ2=makeQuery(id+"F16.imprint","INTERSECT",VERTEX,{"disambiguationData":[OD(0.0)],"derivedFrom":[subQ1,subQ0]});Q4=makeQuery(id+"F16.imprint","IMPRINT",FACE,{"disambiguationData":[TD([[makeQuery(id+"F16.imprint","IMPRINT",EDGE,{"disambiguationData":[TD([[subQ2,1.0]])],"derivedFrom":subQ1}),1.0]])]});}
            var Q5;
            {var subQ0=sQuery(id+"F16.wireOp",EDGE,"E84");var subQ1=sQuery(id+"F16.wireOp",EDGE,"E79");var subQ2=makeQuery(id+"F16.imprint","INTERSECT",VERTEX,{"disambiguationData":[OD(0.0)],"derivedFrom":[subQ1,subQ0]});Q5=makeQuery(id+"F16.imprint","IMPRINT",FACE,{"disambiguationData":[TD([[makeQuery(id+"F16.imprint","IMPRINT",EDGE,{"disambiguationData":[TD([[subQ2,-1.0]])],"derivedFrom":subQ1}),1.0]])]});}
            var Q6;
            {var subQ0=sQuery(id+"F16.wireOp",EDGE,"E84");var subQ1=sQuery(id+"F16.wireOp",EDGE,"E83.5.0");var subQ2=makeQuery(id+"F16.imprint","INTERSECT",VERTEX,{"disambiguationData":[OD(0.0)],"derivedFrom":[subQ1,subQ0]});Q6=makeQuery(id+"F16.imprint","IMPRINT",FACE,{"disambiguationData":[TD([[makeQuery(id+"F16.imprint","IMPRINT",EDGE,{"disambiguationData":[TD([[subQ2,1.0]])],"derivedFrom":subQ1}),1.0]])]});}
            extrude(context, id + "F20", {"entities" : qUnion([Q0, Q1, Q2, Q3, Q4, Q5, Q6]), "operationType" : NewBodyOperationType.ADD, "oppositeDirection" : true, "depth" : 26.16 * mm});
        }
        {
            var Q0;
            Q0=qCreatedBy(makeId("Top.planeOp"),FACE);
            var sketch = newSketch(context, id + "F21", { "sketchPlane" : qUnion([Q0])});
            skLineSegment(sketch, "E85", {"start": v(0, 0) * mm, "end": v(70.54, -18.9) * mm, "construction": true});
            skCircle(sketch, "E86", {"center": v(70.54, -18.9) * mm, "radius": 16.51 * mm});
            skCircle(sketch, "E87", {"center": v(70.54, -18.9) * mm, "radius": 3.43 * mm});
            skPoint(sketch, "E88.0", {"position": v(57.11, -57.11) * mm});
            skCircle(sketch, "E89", {"center": v(57.11, -57.11) * mm, "radius": 6.48 * mm});
            skCircle(sketch, "E90.0", {"center": v(57.11, -57.11) * mm, "radius": 3 * mm});
            skSolve(sketch);
        }
        {
            var Q0;
            Q0=qCreatedBy(makeId("Top.planeOp"),FACE);
            var sketch = newSketch(context, id + "F22", { "sketchPlane" : qUnion([Q0])});
            skArc(sketch, "E91.0", {"start": v(38.26, 32.64) * mm, "mid": v(-41.53, 28.36) * mm, "end": v(-16.47, -47.52) * mm});
            skPoint(sketch, "E92.0", {"position": v(70.54, -18.9) * mm});
            skArc(sketch, "E93.0", {"start": v(45.6, -69.04) * mm, "mid": v(60.2, -67.94) * mm, "end": v(69.39, -56.53) * mm});
            skCircle(sketch, "E94.0", {"center": v(40.68, -62.6) * mm, "radius": 1.5 * mm});
            skCircle(sketch, "E95.0", {"center": v(36.67, -47.63) * mm, "radius": 1.5 * mm});
            skCircle(sketch, "E96.0", {"center": v(47.63, -36.67) * mm, "radius": 1.5 * mm});
            skCircle(sketch, "E97.0", {"center": v(62.6, -40.68) * mm, "radius": 1.5 * mm});
            skCircle(sketch, "E98.0", {"center": v(66.6, -55.65) * mm, "radius": 1.5 * mm});
            skCircle(sketch, "E99.0", {"center": v(55.65, -66.6) * mm, "radius": 1.5 * mm});
            skCircle(sketch, "E100.0", {"center": v(57.11, -57.11) * mm, "radius": 5.97 * mm});
            skArc(sketch, "E101", {"start": v(79.1, -21.26) * mm, "mid": v(79.22, -16.97) * mm, "end": v(77.3, -13.13) * mm});
            skLineSegment(sketch, "E102", {"start": v(-16.47, -47.52) * mm, "end": v(45.6, -69.04) * mm});
            skLineSegment(sketch, "E103", {"start": v(69.39, -56.53) * mm, "end": v(79.1, -21.26) * mm});
            skLineSegment(sketch, "E104", {"start": v(77.3, -13.13) * mm, "end": v(38.26, 32.64) * mm});
            skCircle(sketch, "E105.0", {"center": v(70.54, -18.9) * mm, "radius": 3.43 * mm});
            skArc(sketch, "E106", {"start": v(70.54, -33.38) * mm, "mid": v(69.93, -33.37) * mm, "end": v(69.32, -33.33) * mm});
            skArc(sketch, "E107.0", {"start": v(70.54, -34.65) * mm, "mid": v(69.88, -34.63) * mm, "end": v(69.21, -34.6) * mm});
            skArc(sketch, "E108", {"start": v(69.21, -34.6) * mm, "mid": v(68.64, -33.9) * mm, "end": v(69.32, -33.33) * mm});
            skArc(sketch, "E109", {"start": v(70.54, -34.65) * mm, "mid": v(71.17, -34.01) * mm, "end": v(70.54, -33.38) * mm});
            skArc(sketch, "E110", {"start": v(70.54, -34.01) * mm, "mid": v(69.9, -34) * mm, "end": v(69.27, -33.96) * mm, "construction": true});
            skCircle(sketch, "E111.0", {"center": v(0, 0) * mm, "radius": 38.1 * mm});
            skCircle(sketch, "E112.0", {"center": v(0, 41.68) * mm, "radius": 1.9 * mm});
            skArc(sketch, "E113.0.0", {"start": v(42.92, 7.57) * mm, "mid": v(30.82, 30.82) * mm, "end": v(7.57, 42.92) * mm});
            skArc(sketch, "E113.0.1", {"start": v(7.57, 42.92) * mm, "mid": v(5.36, 41.38) * mm, "end": v(6.9, 39.17) * mm});
            skArc(sketch, "E113.0.2", {"start": v(6.9, 39.17) * mm, "mid": v(28.12, 28.12) * mm, "end": v(39.17, 6.9) * mm});
            skArc(sketch, "E113.0.3", {"start": v(39.17, 6.9) * mm, "mid": v(41.38, 5.36) * mm, "end": v(42.92, 7.57) * mm});
            skArc(sketch, "E114.0.0", {"start": v(-42.92, 7.57) * mm, "mid": v(-41.38, 5.36) * mm, "end": v(-39.17, 6.9) * mm});
            skArc(sketch, "E114.0.1", {"start": v(-39.17, 6.9) * mm, "mid": v(-28.12, 28.12) * mm, "end": v(-6.9, 39.17) * mm});
            skArc(sketch, "E114.0.2", {"start": v(-6.9, 39.17) * mm, "mid": v(-5.36, 41.38) * mm, "end": v(-7.57, 42.92) * mm});
            skArc(sketch, "E114.0.3", {"start": v(-7.57, 42.92) * mm, "mid": v(-30.82, 30.82) * mm, "end": v(-42.92, 7.57) * mm});
            skCircle(sketch, "E115.0", {"center": v(41.68, 0) * mm, "radius": 1.9 * mm});
            skArc(sketch, "E116.0.0", {"start": v(42.92, -7.57) * mm, "mid": v(41.38, -5.36) * mm, "end": v(39.17, -6.9) * mm});
            skArc(sketch, "E116.0.1", {"start": v(39.17, -6.9) * mm, "mid": v(28.12, -28.12) * mm, "end": v(6.9, -39.17) * mm});
            skArc(sketch, "E116.0.2", {"start": v(6.9, -39.17) * mm, "mid": v(5.36, -41.38) * mm, "end": v(7.57, -42.92) * mm});
            skArc(sketch, "E116.0.3", {"start": v(7.57, -42.92) * mm, "mid": v(30.82, -30.82) * mm, "end": v(42.92, -7.57) * mm});
            skCircle(sketch, "E117.0", {"center": v(-41.68, 0) * mm, "radius": 1.9 * mm});
            skArc(sketch, "E118.0.0", {"start": v(-7.57, -42.92) * mm, "mid": v(-5.36, -41.38) * mm, "end": v(-6.9, -39.17) * mm});
            skArc(sketch, "E118.0.1", {"start": v(-6.9, -39.17) * mm, "mid": v(-28.12, -28.12) * mm, "end": v(-39.17, -6.9) * mm});
            skArc(sketch, "E118.0.2", {"start": v(-39.17, -6.9) * mm, "mid": v(-41.38, -5.36) * mm, "end": v(-42.92, -7.57) * mm});
            skArc(sketch, "E118.0.3", {"start": v(-42.92, -7.57) * mm, "mid": v(-30.82, -30.82) * mm, "end": v(-7.57, -42.92) * mm});
            skCircle(sketch, "E119.0", {"center": v(0, -41.68) * mm, "radius": 1.9 * mm});
            skSolve(sketch);
        }
        {
            var Q0;
            Q0=makeQuery(id+"F22.imprint","IMPRINT",FACE,{"disambiguationData":[TD([[makeQuery(id+"F22.imprint","IMPRINT",EDGE,{"derivedFrom":sQuery(id+"F22.wireOp",EDGE,"E91.0")}),1.0]])]});
            extrude(context, id + "F23", {"entities" : qUnion([Q0]), "depth" : 3.17 * mm});
        }
        {
            var Q0;
            Q0=makeQuery(id+"F21.imprint","IMPRINT",FACE,{"disambiguationData":[TD([[makeQuery(id+"F21.imprint","IMPRINT",EDGE,{"derivedFrom":sQuery(id+"F21.wireOp",EDGE,"E86")}),1.0]])]});
            extrude(context, id + "F24", {"entities" : qUnion([Q0]), "depth" : 11.43 * mm});
        }
        {
            var Q0;
            Q0=makeQuery(id+"F21.imprint","IMPRINT",FACE,{"disambiguationData":[TD([[makeQuery(id+"F21.imprint","IMPRINT",EDGE,{"derivedFrom":sQuery(id+"F21.wireOp",EDGE,"E89")}),1.0]])]});
            extrude(context, id + "F25", {"entities" : qUnion([Q0]), "depth" : 11.43 * mm});
        }
        {
            var Q0;
            Q0=qCreatedBy(makeId("Top.planeOp"),FACE);
            var sketch = newSketch(context, id + "F26", { "sketchPlane" : qUnion([Q0])});
            skCircle(sketch, "E120", {"center": v(0, 0) * mm, "radius": 3.43 * mm});
            skCircle(sketch, "E121", {"center": v(0, 0) * mm, "radius": 8.26 * mm});
            skCircle(sketch, "E122", {"center": v(0, 0) * mm, "radius": 2.54 * mm});
            skSolve(sketch);
        }
        {
            var Q0;
            Q0=makeQuery(id+"F26.imprint","IMPRINT",FACE,{"disambiguationData":[TD([[makeQuery(id+"F26.imprint","IMPRINT",EDGE,{"derivedFrom":sQuery(id+"F26.wireOp",EDGE,"E120")}),-1.0]])]});
            var Q1;
            Q1=makeQuery(id+"F26.imprint","IMPRINT",FACE,{"disambiguationData":[TD([[makeQuery(id+"F26.imprint","IMPRINT",EDGE,{"derivedFrom":sQuery(id+"F26.wireOp",EDGE,"E120")}),1.0]])]});
            var Q2;
            Q2=makeQuery(id+"F26.imprint","IMPRINT",FACE,{"disambiguationData":[TD([[makeQuery(id+"F26.imprint","IMPRINT",EDGE,{"derivedFrom":sQuery(id+"F26.wireOp",EDGE,"E122")}),1.0]])]});
            extrude(context, id + "F27", {"entities" : qUnion([Q0, Q1, Q2]), "oppositeDirection" : true, "depth" : 9.14 * mm});
        }
        {
            var Q0;
            Q0=makeQuery(id+"F26.imprint","IMPRINT",FACE,{"disambiguationData":[TD([[makeQuery(id+"F26.imprint","IMPRINT",EDGE,{"derivedFrom":sQuery(id+"F26.wireOp",EDGE,"E122")}),1.0]])]});
            var Q1;
            Q1=makeQuery(id+"F26.imprint","IMPRINT",FACE,{"disambiguationData":[TD([[makeQuery(id+"F26.imprint","IMPRINT",EDGE,{"derivedFrom":sQuery(id+"F26.wireOp",EDGE,"E120")}),1.0]])]});
            extrude(context, id + "F28", {"entities" : qUnion([Q0, Q1]), "operationType" : NewBodyOperationType.ADD, "depth" : 6.6 * mm});
        }
        {
            var Q0;
            Q0=makeQuery(id+"F26.imprint","IMPRINT",FACE,{"disambiguationData":[TD([[makeQuery(id+"F26.imprint","IMPRINT",EDGE,{"derivedFrom":sQuery(id+"F26.wireOp",EDGE,"E122")}),1.0]])]});
            extrude(context, id + "F29", {"entities" : qUnion([Q0]), "operationType" : NewBodyOperationType.ADD, "depth" : 15.24 * mm});
        }
    });
